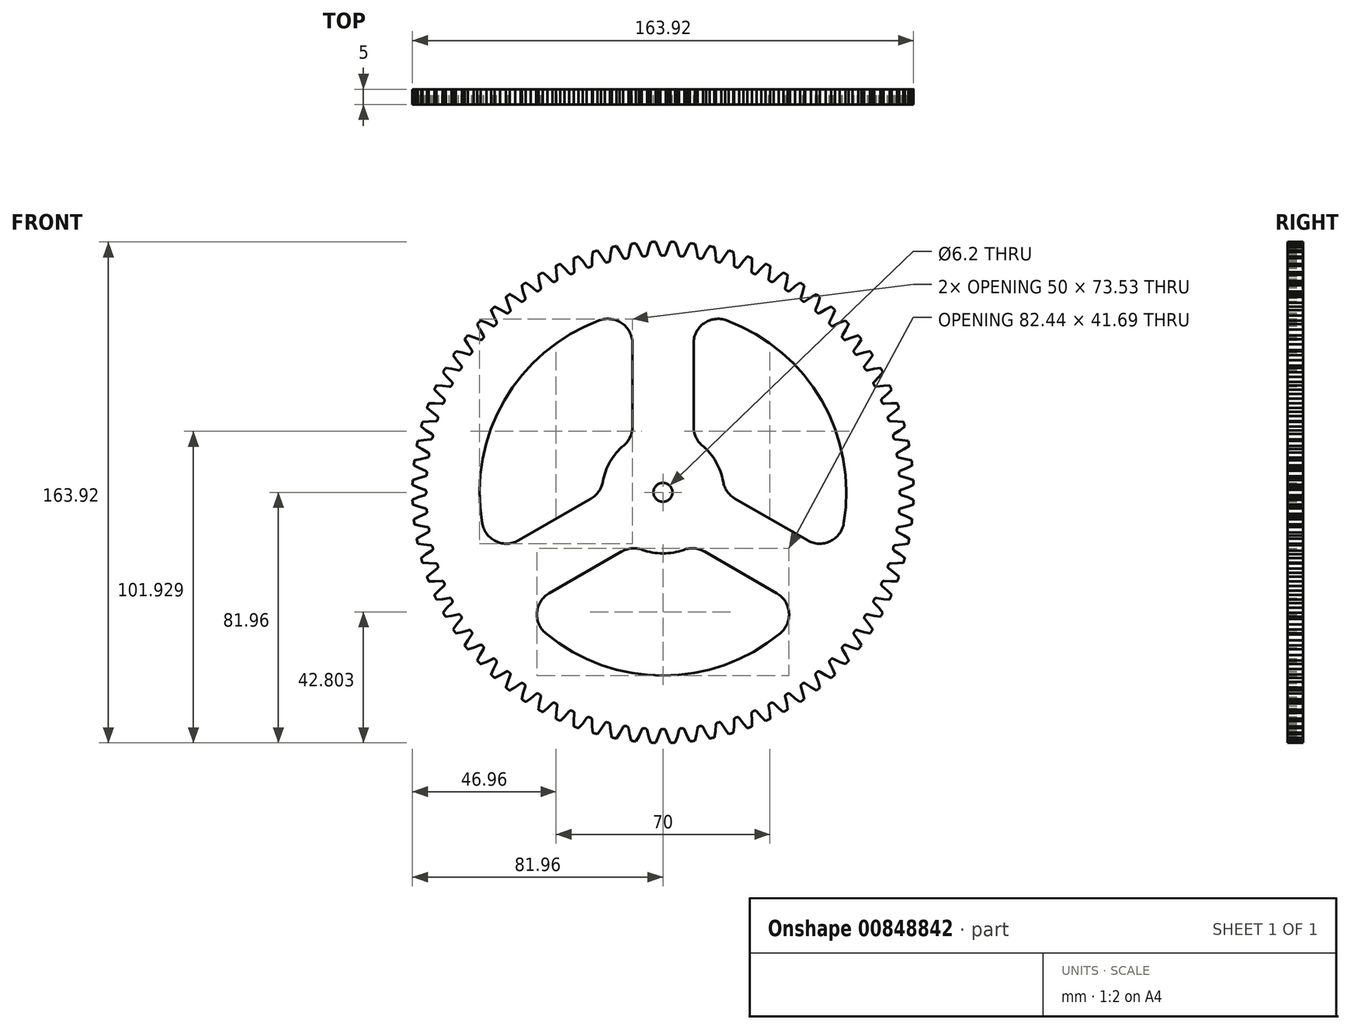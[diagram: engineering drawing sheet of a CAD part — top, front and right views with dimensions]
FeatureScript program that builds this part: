
annotation { "Feature Type Name" : "Feature", "Feature Type Description" : "" }
export const myFeature = defineFeature(function(context is Context, id is Id, definition is map)
    precondition{}
    {
        {
            var Q0;
            Q0=qCreatedBy(makeId("Front.planeOp"),FACE);
            var sketch = newSketch(context, id + "F0", { "sketchPlane" : qUnion([Q0])});
            skArc(sketch, "E0", {"start": v(-10, 21.45) * mm, "mid": v(-10.75, 18.07) * mm, "end": v(-12.86, 15.32) * mm});
            skLineSegment(sketch, "E1", {"start": v(-10, 48.79) * mm, "end": v(-10, 21.45) * mm});
            skArc(sketch, "E2", {"start": v(-20.77, 56.3) * mm, "mid": v(-13.43, 55.35) * mm, "end": v(-10, 48.79) * mm});
            skArc(sketch, "E3", {"start": v(-59.13, -10.16) * mm, "mid": v(-51.96, 30) * mm, "end": v(-20.77, 56.3) * mm});
            skArc(sketch, "E4", {"start": v(-47.25, -15.73) * mm, "mid": v(-54.65, -16.05) * mm, "end": v(-59.13, -10.16) * mm});
            skLineSegment(sketch, "E5", {"start": v(-47.25, -15.73) * mm, "end": v(-23.57, -2.06) * mm});
            skArc(sketch, "E6", {"start": v(-19.7, 3.47) * mm, "mid": v(-21.02, 0.28) * mm, "end": v(-23.57, -2.06) * mm});
            skArc(sketch, "E7", {"start": v(-19.7, 3.47) * mm, "mid": v(-17.32, 10) * mm, "end": v(-12.86, 15.32) * mm});
            skArc(sketch, "E8", {"start": v(-65.95, 40.7) * mm, "mid": v(-66.08, 40.5) * mm, "end": v(-66.2, 40.28) * mm});
            skArc(sketch, "E9", {"start": v(-65.95, 40.7) * mm, "mid": v(-65.85, 41.12) * mm, "end": v(-66.03, 41.5) * mm});
            skLineSegment(sketch, "E10", {"start": v(-67.47, 43.26) * mm, "end": v(-68.62, 44.9) * mm});
            skLineSegment(sketch, "E11", {"start": v(-66.03, 41.5) * mm, "end": v(-67.47, 43.26) * mm});
            skArc(sketch, "E12", {"start": v(-67.74, 46.22) * mm, "mid": v(-68.18, 45.56) * mm, "end": v(-68.62, 44.9) * mm});
            skLineSegment(sketch, "E13", {"start": v(-65.79, 45.78) * mm, "end": v(-67.74, 46.22) * mm});
            skLineSegment(sketch, "E14", {"start": v(-63.61, 45.12) * mm, "end": v(-65.79, 45.78) * mm});
            skArc(sketch, "E15", {"start": v(-63.61, 45.12) * mm, "mid": v(-63.19, 45.1) * mm, "end": v(-62.84, 45.35) * mm});
            skArc(sketch, "E16", {"start": v(-62.55, 45.75) * mm, "mid": v(-62.7, 45.55) * mm, "end": v(-62.84, 45.35) * mm});
            skArc(sketch, "E17", {"start": v(-62.55, 45.75) * mm, "mid": v(-62.42, 46.16) * mm, "end": v(-62.57, 46.56) * mm});
            skLineSegment(sketch, "E18", {"start": v(-63.87, 48.42) * mm, "end": v(-64.89, 50.14) * mm});
            skLineSegment(sketch, "E19", {"start": v(-62.57, 46.56) * mm, "end": v(-63.87, 48.42) * mm});
            skArc(sketch, "E20", {"start": v(-63.9, 51.39) * mm, "mid": v(-64.4, 50.77) * mm, "end": v(-64.89, 50.14) * mm});
            skLineSegment(sketch, "E21", {"start": v(-62, 50.8) * mm, "end": v(-63.9, 51.39) * mm});
            skLineSegment(sketch, "E22", {"start": v(-59.88, 49.97) * mm, "end": v(-62, 50.8) * mm});
            skArc(sketch, "E23", {"start": v(-59.88, 49.97) * mm, "mid": v(-59.46, 49.92) * mm, "end": v(-59.1, 50.14) * mm});
            skArc(sketch, "E24", {"start": v(-58.77, 50.52) * mm, "mid": v(-58.93, 50.33) * mm, "end": v(-59.1, 50.14) * mm});
            skArc(sketch, "E25", {"start": v(-58.77, 50.52) * mm, "mid": v(-58.61, 50.91) * mm, "end": v(-58.72, 51.32) * mm});
            skLineSegment(sketch, "E26", {"start": v(-59.88, 53.28) * mm, "end": v(-60.75, 55.08) * mm});
            skLineSegment(sketch, "E27", {"start": v(-58.72, 51.32) * mm, "end": v(-59.88, 53.28) * mm});
            skArc(sketch, "E28", {"start": v(-59.67, 56.24) * mm, "mid": v(-60.21, 55.66) * mm, "end": v(-60.75, 55.08) * mm});
            skLineSegment(sketch, "E29", {"start": v(-57.81, 55.51) * mm, "end": v(-59.67, 56.24) * mm});
            skLineSegment(sketch, "E30", {"start": v(-55.77, 54.51) * mm, "end": v(-57.81, 55.51) * mm});
            skArc(sketch, "E31", {"start": v(-55.77, 54.51) * mm, "mid": v(-55.36, 54.43) * mm, "end": v(-54.98, 54.63) * mm});
            skArc(sketch, "E32", {"start": v(-54.63, 54.98) * mm, "mid": v(-54.8, 54.8) * mm, "end": v(-54.98, 54.63) * mm});
            skArc(sketch, "E33", {"start": v(-54.63, 54.98) * mm, "mid": v(-54.43, 55.36) * mm, "end": v(-54.51, 55.77) * mm});
            skLineSegment(sketch, "E34", {"start": v(-55.51, 57.81) * mm, "end": v(-56.24, 59.67) * mm});
            skLineSegment(sketch, "E35", {"start": v(-54.51, 55.77) * mm, "end": v(-55.51, 57.81) * mm});
            skArc(sketch, "E36", {"start": v(-55.08, 60.75) * mm, "mid": v(-55.66, 60.21) * mm, "end": v(-56.24, 59.67) * mm});
            skLineSegment(sketch, "E37", {"start": v(-53.28, 59.88) * mm, "end": v(-55.08, 60.75) * mm});
            skLineSegment(sketch, "E38", {"start": v(-51.32, 58.72) * mm, "end": v(-53.28, 59.88) * mm});
            skArc(sketch, "E39", {"start": v(-51.32, 58.72) * mm, "mid": v(-50.91, 58.61) * mm, "end": v(-50.52, 58.77) * mm});
            skArc(sketch, "E40", {"start": v(-50.14, 59.1) * mm, "mid": v(-50.33, 58.93) * mm, "end": v(-50.52, 58.77) * mm});
            skArc(sketch, "E41", {"start": v(-50.14, 59.1) * mm, "mid": v(-49.92, 59.46) * mm, "end": v(-49.97, 59.88) * mm});
            skLineSegment(sketch, "E42", {"start": v(-50.8, 62) * mm, "end": v(-51.39, 63.9) * mm});
            skLineSegment(sketch, "E43", {"start": v(-49.97, 59.88) * mm, "end": v(-50.8, 62) * mm});
            skArc(sketch, "E44", {"start": v(-50.14, 64.89) * mm, "mid": v(-50.77, 64.4) * mm, "end": v(-51.39, 63.9) * mm});
            skLineSegment(sketch, "E45", {"start": v(-48.42, 63.87) * mm, "end": v(-50.14, 64.89) * mm});
            skLineSegment(sketch, "E46", {"start": v(-46.56, 62.57) * mm, "end": v(-48.42, 63.87) * mm});
            skArc(sketch, "E47", {"start": v(-46.56, 62.57) * mm, "mid": v(-46.16, 62.42) * mm, "end": v(-45.75, 62.55) * mm});
            skArc(sketch, "E48", {"start": v(-45.35, 62.84) * mm, "mid": v(-45.55, 62.7) * mm, "end": v(-45.75, 62.55) * mm});
            skArc(sketch, "E49", {"start": v(-45.35, 62.84) * mm, "mid": v(-45.1, 63.19) * mm, "end": v(-45.12, 63.61) * mm});
            skLineSegment(sketch, "E50", {"start": v(-45.78, 65.79) * mm, "end": v(-46.22, 67.74) * mm});
            skLineSegment(sketch, "E51", {"start": v(-45.12, 63.61) * mm, "end": v(-45.78, 65.79) * mm});
            skArc(sketch, "E52", {"start": v(-44.9, 68.62) * mm, "mid": v(-45.56, 68.18) * mm, "end": v(-46.22, 67.74) * mm});
            skLineSegment(sketch, "E53", {"start": v(-43.26, 67.47) * mm, "end": v(-44.9, 68.62) * mm});
            skLineSegment(sketch, "E54", {"start": v(-41.5, 66.03) * mm, "end": v(-43.26, 67.47) * mm});
            skArc(sketch, "E55", {"start": v(-41.5, 66.03) * mm, "mid": v(-41.12, 65.85) * mm, "end": v(-40.7, 65.95) * mm});
            skArc(sketch, "E56", {"start": v(-40.28, 66.2) * mm, "mid": v(-40.5, 66.08) * mm, "end": v(-40.7, 65.95) * mm});
            skArc(sketch, "E57", {"start": v(-40.28, 66.2) * mm, "mid": v(-40, 66.53) * mm, "end": v(-39.99, 66.96) * mm});
            skLineSegment(sketch, "E58", {"start": v(-40.48, 69.17) * mm, "end": v(-40.76, 71.15) * mm});
            skLineSegment(sketch, "E59", {"start": v(-39.99, 66.96) * mm, "end": v(-40.48, 69.17) * mm});
            skArc(sketch, "E60", {"start": v(-39.37, 71.93) * mm, "mid": v(-40.07, 71.54) * mm, "end": v(-40.76, 71.15) * mm});
            skLineSegment(sketch, "E61", {"start": v(-37.83, 70.66) * mm, "end": v(-39.37, 71.93) * mm});
            skLineSegment(sketch, "E62", {"start": v(-36.2, 69.08) * mm, "end": v(-37.83, 70.66) * mm});
            skArc(sketch, "E63", {"start": v(-36.2, 69.08) * mm, "mid": v(-35.82, 68.88) * mm, "end": v(-35.4, 68.94) * mm});
            skArc(sketch, "E64", {"start": v(-34.96, 69.17) * mm, "mid": v(-35.18, 69.05) * mm, "end": v(-35.4, 68.94) * mm});
            skArc(sketch, "E65", {"start": v(-34.96, 69.17) * mm, "mid": v(-34.66, 69.47) * mm, "end": v(-34.6, 69.89) * mm});
            skLineSegment(sketch, "E66", {"start": v(-34.93, 72.14) * mm, "end": v(-35.05, 74.13) * mm});
            skLineSegment(sketch, "E67", {"start": v(-34.6, 69.89) * mm, "end": v(-34.93, 72.14) * mm});
            skArc(sketch, "E68", {"start": v(-33.6, 74.8) * mm, "mid": v(-34.33, 74.47) * mm, "end": v(-35.05, 74.13) * mm});
            skLineSegment(sketch, "E69", {"start": v(-32.17, 73.4) * mm, "end": v(-33.6, 74.8) * mm});
            skLineSegment(sketch, "E70", {"start": v(-30.67, 71.7) * mm, "end": v(-32.17, 73.4) * mm});
            skArc(sketch, "E71", {"start": v(-30.67, 71.7) * mm, "mid": v(-30.31, 71.47) * mm, "end": v(-29.89, 71.5) * mm});
            skArc(sketch, "E72", {"start": v(-29.43, 71.7) * mm, "mid": v(-29.66, 71.6) * mm, "end": v(-29.89, 71.5) * mm});
            skArc(sketch, "E73", {"start": v(-29.43, 71.7) * mm, "mid": v(-29.1, 71.97) * mm, "end": v(-29.02, 72.39) * mm});
            skLineSegment(sketch, "E74", {"start": v(-29.16, 74.66) * mm, "end": v(-29.13, 76.65) * mm});
            skLineSegment(sketch, "E75", {"start": v(-29.02, 72.39) * mm, "end": v(-29.16, 74.66) * mm});
            skArc(sketch, "E76", {"start": v(-27.63, 77.2) * mm, "mid": v(-28.38, 76.93) * mm, "end": v(-29.13, 76.65) * mm});
            skLineSegment(sketch, "E77", {"start": v(-26.31, 75.7) * mm, "end": v(-27.63, 77.2) * mm});
            skLineSegment(sketch, "E78", {"start": v(-24.95, 73.9) * mm, "end": v(-26.31, 75.7) * mm});
            skArc(sketch, "E79", {"start": v(-24.95, 73.9) * mm, "mid": v(-24.6, 73.63) * mm, "end": v(-24.18, 73.63) * mm});
            skArc(sketch, "E80", {"start": v(-23.71, 73.78) * mm, "mid": v(-23.95, 73.7) * mm, "end": v(-24.18, 73.63) * mm});
            skArc(sketch, "E81", {"start": v(-23.71, 73.78) * mm, "mid": v(-23.37, 74.03) * mm, "end": v(-23.25, 74.44) * mm});
            skLineSegment(sketch, "E82", {"start": v(-23.21, 76.71) * mm, "end": v(-23.02, 78.7) * mm});
            skLineSegment(sketch, "E83", {"start": v(-23.25, 74.44) * mm, "end": v(-23.21, 76.71) * mm});
            skArc(sketch, "E84", {"start": v(-21.5, 79.13) * mm, "mid": v(-22.26, 78.92) * mm, "end": v(-23.02, 78.7) * mm});
            skLineSegment(sketch, "E85", {"start": v(-20.29, 77.54) * mm, "end": v(-21.5, 79.13) * mm});
            skLineSegment(sketch, "E86", {"start": v(-19.07, 75.62) * mm, "end": v(-20.29, 77.54) * mm});
            skArc(sketch, "E87", {"start": v(-19.07, 75.62) * mm, "mid": v(-18.76, 75.34) * mm, "end": v(-18.33, 75.3) * mm});
            skArc(sketch, "E88", {"start": v(-17.85, 75.42) * mm, "mid": v(-18.1, 75.36) * mm, "end": v(-18.33, 75.3) * mm});
            skArc(sketch, "E89", {"start": v(-17.85, 75.42) * mm, "mid": v(-17.5, 75.64) * mm, "end": v(-17.34, 76.04) * mm});
            skLineSegment(sketch, "E90", {"start": v(-17.12, 78.3) * mm, "end": v(-16.78, 80.27) * mm});
            skLineSegment(sketch, "E91", {"start": v(-17.34, 76.04) * mm, "end": v(-17.12, 78.3) * mm});
            skArc(sketch, "E92", {"start": v(-15.22, 80.58) * mm, "mid": v(-16, 80.42) * mm, "end": v(-16.78, 80.27) * mm});
            skLineSegment(sketch, "E93", {"start": v(-14.14, 78.9) * mm, "end": v(-15.22, 80.58) * mm});
            skLineSegment(sketch, "E94", {"start": v(-13.08, 76.88) * mm, "end": v(-14.14, 78.9) * mm});
            skArc(sketch, "E95", {"start": v(-13.08, 76.88) * mm, "mid": v(-12.79, 76.58) * mm, "end": v(-12.37, 76.5) * mm});
            skArc(sketch, "E96", {"start": v(-11.88, 76.58) * mm, "mid": v(-12.12, 76.55) * mm, "end": v(-12.37, 76.5) * mm});
            skArc(sketch, "E97", {"start": v(-11.88, 76.58) * mm, "mid": v(-11.5, 76.78) * mm, "end": v(-11.32, 77.16) * mm});
            skLineSegment(sketch, "E98", {"start": v(-10.93, 79.4) * mm, "end": v(-10.43, 81.33) * mm});
            skLineSegment(sketch, "E99", {"start": v(-11.32, 77.16) * mm, "end": v(-10.93, 79.4) * mm});
            skArc(sketch, "E100", {"start": v(-8.85, 81.52) * mm, "mid": v(-9.64, 81.43) * mm, "end": v(-10.43, 81.33) * mm});
            skLineSegment(sketch, "E101", {"start": v(-7.9, 79.76) * mm, "end": v(-8.85, 81.52) * mm});
            skLineSegment(sketch, "E102", {"start": v(-7, 77.67) * mm, "end": v(-7.9, 79.76) * mm});
            skArc(sketch, "E103", {"start": v(-7, 77.67) * mm, "mid": v(-6.74, 77.34) * mm, "end": v(-6.33, 77.24) * mm});
            skArc(sketch, "E104", {"start": v(-5.83, 77.28) * mm, "mid": v(-6.08, 77.26) * mm, "end": v(-6.33, 77.24) * mm});
            skArc(sketch, "E105", {"start": v(-5.83, 77.28) * mm, "mid": v(-5.44, 77.45) * mm, "end": v(-5.23, 77.81) * mm});
            skLineSegment(sketch, "E106", {"start": v(-4.66, 80.01) * mm, "end": v(-4.01, 81.9) * mm});
            skLineSegment(sketch, "E107", {"start": v(-5.23, 77.81) * mm, "end": v(-4.66, 80.01) * mm});
            skArc(sketch, "E108", {"start": v(-2.42, 81.96) * mm, "mid": v(-3.22, 81.94) * mm, "end": v(-4.01, 81.9) * mm});
            skLineSegment(sketch, "E109", {"start": v(-1.63, 80.13) * mm, "end": v(-2.42, 81.96) * mm});
            skLineSegment(sketch, "E110", {"start": v(-0.9, 77.98) * mm, "end": v(-1.63, 80.13) * mm});
            skArc(sketch, "E111", {"start": v(-0.9, 77.98) * mm, "mid": v(-0.65, 77.63) * mm, "end": v(-0.25, 77.5) * mm});
            skArc(sketch, "E112", {"start": v(0.25, 77.5) * mm, "mid": v(0, 77.5) * mm, "end": v(-0.25, 77.5) * mm});
            skArc(sketch, "E113", {"start": v(0.25, 77.5) * mm, "mid": v(0.65, 77.63) * mm, "end": v(0.9, 77.98) * mm});
            skLineSegment(sketch, "E114", {"start": v(1.63, 80.13) * mm, "end": v(2.42, 81.96) * mm});
            skLineSegment(sketch, "E115", {"start": v(0.9, 77.98) * mm, "end": v(1.63, 80.13) * mm});
            skArc(sketch, "E116", {"start": v(4.01, 81.9) * mm, "mid": v(3.22, 81.94) * mm, "end": v(2.42, 81.96) * mm});
            skLineSegment(sketch, "E117", {"start": v(4.66, 80.01) * mm, "end": v(4.01, 81.9) * mm});
            skLineSegment(sketch, "E118", {"start": v(5.23, 77.81) * mm, "end": v(4.66, 80.01) * mm});
            skArc(sketch, "E119", {"start": v(5.23, 77.81) * mm, "mid": v(5.44, 77.45) * mm, "end": v(5.83, 77.28) * mm});
            skArc(sketch, "E120", {"start": v(6.33, 77.24) * mm, "mid": v(6.08, 77.26) * mm, "end": v(5.83, 77.28) * mm});
            skArc(sketch, "E121", {"start": v(6.33, 77.24) * mm, "mid": v(6.74, 77.34) * mm, "end": v(7, 77.67) * mm});
            skLineSegment(sketch, "E122", {"start": v(7.9, 79.76) * mm, "end": v(8.85, 81.52) * mm});
            skLineSegment(sketch, "E123", {"start": v(7, 77.67) * mm, "end": v(7.9, 79.76) * mm});
            skArc(sketch, "E124", {"start": v(10.43, 81.33) * mm, "mid": v(9.64, 81.43) * mm, "end": v(8.85, 81.52) * mm});
            skLineSegment(sketch, "E125", {"start": v(10.93, 79.4) * mm, "end": v(10.43, 81.33) * mm});
            skLineSegment(sketch, "E126", {"start": v(11.32, 77.16) * mm, "end": v(10.93, 79.4) * mm});
            skArc(sketch, "E127", {"start": v(11.32, 77.16) * mm, "mid": v(11.5, 76.78) * mm, "end": v(11.88, 76.58) * mm});
            skArc(sketch, "E128", {"start": v(12.37, 76.5) * mm, "mid": v(12.12, 76.55) * mm, "end": v(11.88, 76.58) * mm});
            skArc(sketch, "E129", {"start": v(12.37, 76.5) * mm, "mid": v(12.79, 76.58) * mm, "end": v(13.08, 76.88) * mm});
            skLineSegment(sketch, "E130", {"start": v(14.14, 78.9) * mm, "end": v(15.22, 80.58) * mm});
            skLineSegment(sketch, "E131", {"start": v(13.08, 76.88) * mm, "end": v(14.14, 78.9) * mm});
            skArc(sketch, "E132", {"start": v(16.78, 80.27) * mm, "mid": v(16, 80.42) * mm, "end": v(15.22, 80.58) * mm});
            skLineSegment(sketch, "E133", {"start": v(17.12, 78.3) * mm, "end": v(16.78, 80.27) * mm});
            skLineSegment(sketch, "E134", {"start": v(17.34, 76.04) * mm, "end": v(17.12, 78.3) * mm});
            skArc(sketch, "E135", {"start": v(17.34, 76.04) * mm, "mid": v(17.5, 75.64) * mm, "end": v(17.85, 75.42) * mm});
            skArc(sketch, "E136", {"start": v(18.33, 75.3) * mm, "mid": v(18.1, 75.36) * mm, "end": v(17.85, 75.42) * mm});
            skArc(sketch, "E137", {"start": v(18.33, 75.3) * mm, "mid": v(18.76, 75.34) * mm, "end": v(19.07, 75.62) * mm});
            skLineSegment(sketch, "E138", {"start": v(20.29, 77.54) * mm, "end": v(21.5, 79.13) * mm});
            skLineSegment(sketch, "E139", {"start": v(19.07, 75.62) * mm, "end": v(20.29, 77.54) * mm});
            skArc(sketch, "E140", {"start": v(23.02, 78.7) * mm, "mid": v(22.26, 78.92) * mm, "end": v(21.5, 79.13) * mm});
            skLineSegment(sketch, "E141", {"start": v(23.21, 76.71) * mm, "end": v(23.02, 78.7) * mm});
            skLineSegment(sketch, "E142", {"start": v(23.25, 74.44) * mm, "end": v(23.21, 76.71) * mm});
            skArc(sketch, "E143", {"start": v(23.25, 74.44) * mm, "mid": v(23.37, 74.03) * mm, "end": v(23.71, 73.78) * mm});
            skArc(sketch, "E144", {"start": v(24.18, 73.63) * mm, "mid": v(23.95, 73.7) * mm, "end": v(23.71, 73.78) * mm});
            skArc(sketch, "E145", {"start": v(24.18, 73.63) * mm, "mid": v(24.6, 73.63) * mm, "end": v(24.95, 73.9) * mm});
            skLineSegment(sketch, "E146", {"start": v(26.31, 75.7) * mm, "end": v(27.63, 77.2) * mm});
            skLineSegment(sketch, "E147", {"start": v(24.95, 73.9) * mm, "end": v(26.31, 75.7) * mm});
            skArc(sketch, "E148", {"start": v(29.13, 76.65) * mm, "mid": v(28.38, 76.93) * mm, "end": v(27.63, 77.2) * mm});
            skLineSegment(sketch, "E149", {"start": v(29.16, 74.66) * mm, "end": v(29.13, 76.65) * mm});
            skLineSegment(sketch, "E150", {"start": v(29.02, 72.39) * mm, "end": v(29.16, 74.66) * mm});
            skArc(sketch, "E151", {"start": v(29.02, 72.39) * mm, "mid": v(29.1, 71.97) * mm, "end": v(29.43, 71.7) * mm});
            skArc(sketch, "E152", {"start": v(29.89, 71.5) * mm, "mid": v(29.66, 71.6) * mm, "end": v(29.43, 71.7) * mm});
            skArc(sketch, "E153", {"start": v(29.89, 71.5) * mm, "mid": v(30.31, 71.47) * mm, "end": v(30.67, 71.7) * mm});
            skLineSegment(sketch, "E154", {"start": v(32.17, 73.4) * mm, "end": v(33.6, 74.8) * mm});
            skLineSegment(sketch, "E155", {"start": v(30.67, 71.7) * mm, "end": v(32.17, 73.4) * mm});
            skArc(sketch, "E156", {"start": v(35.05, 74.13) * mm, "mid": v(34.33, 74.47) * mm, "end": v(33.6, 74.8) * mm});
            skLineSegment(sketch, "E157", {"start": v(34.93, 72.14) * mm, "end": v(35.05, 74.13) * mm});
            skLineSegment(sketch, "E158", {"start": v(34.6, 69.89) * mm, "end": v(34.93, 72.14) * mm});
            skArc(sketch, "E159", {"start": v(34.6, 69.89) * mm, "mid": v(34.66, 69.47) * mm, "end": v(34.96, 69.17) * mm});
            skArc(sketch, "E160", {"start": v(35.4, 68.94) * mm, "mid": v(35.18, 69.05) * mm, "end": v(34.96, 69.17) * mm});
            skArc(sketch, "E161", {"start": v(35.4, 68.94) * mm, "mid": v(35.82, 68.88) * mm, "end": v(36.2, 69.08) * mm});
            skLineSegment(sketch, "E162", {"start": v(37.83, 70.66) * mm, "end": v(39.37, 71.93) * mm});
            skLineSegment(sketch, "E163", {"start": v(36.2, 69.08) * mm, "end": v(37.83, 70.66) * mm});
            skArc(sketch, "E164", {"start": v(40.76, 71.15) * mm, "mid": v(40.07, 71.54) * mm, "end": v(39.37, 71.93) * mm});
            skLineSegment(sketch, "E165", {"start": v(40.48, 69.17) * mm, "end": v(40.76, 71.15) * mm});
            skLineSegment(sketch, "E166", {"start": v(39.99, 66.96) * mm, "end": v(40.48, 69.17) * mm});
            skArc(sketch, "E167", {"start": v(39.99, 66.96) * mm, "mid": v(40, 66.53) * mm, "end": v(40.28, 66.2) * mm});
            skArc(sketch, "E168", {"start": v(40.7, 65.95) * mm, "mid": v(40.5, 66.08) * mm, "end": v(40.28, 66.2) * mm});
            skArc(sketch, "E169", {"start": v(40.7, 65.95) * mm, "mid": v(41.12, 65.85) * mm, "end": v(41.5, 66.03) * mm});
            skLineSegment(sketch, "E170", {"start": v(43.26, 67.47) * mm, "end": v(44.9, 68.62) * mm});
            skLineSegment(sketch, "E171", {"start": v(41.5, 66.03) * mm, "end": v(43.26, 67.47) * mm});
            skArc(sketch, "E172", {"start": v(46.22, 67.74) * mm, "mid": v(45.56, 68.18) * mm, "end": v(44.9, 68.62) * mm});
            skLineSegment(sketch, "E173", {"start": v(45.78, 65.79) * mm, "end": v(46.22, 67.74) * mm});
            skLineSegment(sketch, "E174", {"start": v(45.12, 63.61) * mm, "end": v(45.78, 65.79) * mm});
            skArc(sketch, "E175", {"start": v(45.12, 63.61) * mm, "mid": v(45.1, 63.19) * mm, "end": v(45.35, 62.84) * mm});
            skArc(sketch, "E176", {"start": v(45.75, 62.55) * mm, "mid": v(45.55, 62.7) * mm, "end": v(45.35, 62.84) * mm});
            skArc(sketch, "E177", {"start": v(45.75, 62.55) * mm, "mid": v(46.16, 62.42) * mm, "end": v(46.56, 62.57) * mm});
            skLineSegment(sketch, "E178", {"start": v(48.42, 63.87) * mm, "end": v(50.14, 64.89) * mm});
            skLineSegment(sketch, "E179", {"start": v(46.56, 62.57) * mm, "end": v(48.42, 63.87) * mm});
            skArc(sketch, "E180", {"start": v(51.39, 63.9) * mm, "mid": v(50.77, 64.4) * mm, "end": v(50.14, 64.89) * mm});
            skLineSegment(sketch, "E181", {"start": v(50.8, 62) * mm, "end": v(51.39, 63.9) * mm});
            skLineSegment(sketch, "E182", {"start": v(49.97, 59.88) * mm, "end": v(50.8, 62) * mm});
            skArc(sketch, "E183", {"start": v(49.97, 59.88) * mm, "mid": v(49.92, 59.46) * mm, "end": v(50.14, 59.1) * mm});
            skArc(sketch, "E184", {"start": v(50.52, 58.77) * mm, "mid": v(50.33, 58.93) * mm, "end": v(50.14, 59.1) * mm});
            skArc(sketch, "E185", {"start": v(50.52, 58.77) * mm, "mid": v(50.91, 58.61) * mm, "end": v(51.32, 58.72) * mm});
            skLineSegment(sketch, "E186", {"start": v(53.28, 59.88) * mm, "end": v(55.08, 60.75) * mm});
            skLineSegment(sketch, "E187", {"start": v(51.32, 58.72) * mm, "end": v(53.28, 59.88) * mm});
            skArc(sketch, "E188", {"start": v(56.24, 59.67) * mm, "mid": v(55.66, 60.21) * mm, "end": v(55.08, 60.75) * mm});
            skLineSegment(sketch, "E189", {"start": v(55.51, 57.81) * mm, "end": v(56.24, 59.67) * mm});
            skLineSegment(sketch, "E190", {"start": v(54.51, 55.77) * mm, "end": v(55.51, 57.81) * mm});
            skArc(sketch, "E191", {"start": v(54.51, 55.77) * mm, "mid": v(54.43, 55.36) * mm, "end": v(54.63, 54.98) * mm});
            skArc(sketch, "E192", {"start": v(54.98, 54.63) * mm, "mid": v(54.8, 54.8) * mm, "end": v(54.63, 54.98) * mm});
            skArc(sketch, "E193", {"start": v(54.98, 54.63) * mm, "mid": v(55.36, 54.43) * mm, "end": v(55.77, 54.51) * mm});
            skLineSegment(sketch, "E194", {"start": v(57.81, 55.51) * mm, "end": v(59.67, 56.24) * mm});
            skLineSegment(sketch, "E195", {"start": v(55.77, 54.51) * mm, "end": v(57.81, 55.51) * mm});
            skArc(sketch, "E196", {"start": v(60.75, 55.08) * mm, "mid": v(60.21, 55.66) * mm, "end": v(59.67, 56.24) * mm});
            skLineSegment(sketch, "E197", {"start": v(59.88, 53.28) * mm, "end": v(60.75, 55.08) * mm});
            skLineSegment(sketch, "E198", {"start": v(58.72, 51.32) * mm, "end": v(59.88, 53.28) * mm});
            skArc(sketch, "E199", {"start": v(58.72, 51.32) * mm, "mid": v(58.61, 50.91) * mm, "end": v(58.77, 50.52) * mm});
            skArc(sketch, "E200", {"start": v(59.1, 50.14) * mm, "mid": v(58.93, 50.33) * mm, "end": v(58.77, 50.52) * mm});
            skArc(sketch, "E201", {"start": v(59.1, 50.14) * mm, "mid": v(59.46, 49.92) * mm, "end": v(59.88, 49.97) * mm});
            skLineSegment(sketch, "E202", {"start": v(62, 50.8) * mm, "end": v(63.9, 51.39) * mm});
            skLineSegment(sketch, "E203", {"start": v(59.88, 49.97) * mm, "end": v(62, 50.8) * mm});
            skArc(sketch, "E204", {"start": v(64.89, 50.14) * mm, "mid": v(64.4, 50.77) * mm, "end": v(63.9, 51.39) * mm});
            skLineSegment(sketch, "E205", {"start": v(63.87, 48.42) * mm, "end": v(64.89, 50.14) * mm});
            skLineSegment(sketch, "E206", {"start": v(62.57, 46.56) * mm, "end": v(63.87, 48.42) * mm});
            skArc(sketch, "E207", {"start": v(62.57, 46.56) * mm, "mid": v(62.42, 46.16) * mm, "end": v(62.55, 45.75) * mm});
            skArc(sketch, "E208", {"start": v(62.84, 45.35) * mm, "mid": v(62.7, 45.55) * mm, "end": v(62.55, 45.75) * mm});
            skArc(sketch, "E209", {"start": v(62.84, 45.35) * mm, "mid": v(63.19, 45.1) * mm, "end": v(63.61, 45.12) * mm});
            skLineSegment(sketch, "E210", {"start": v(65.79, 45.78) * mm, "end": v(67.74, 46.22) * mm});
            skLineSegment(sketch, "E211", {"start": v(63.61, 45.12) * mm, "end": v(65.79, 45.78) * mm});
            skArc(sketch, "E212", {"start": v(68.62, 44.9) * mm, "mid": v(68.18, 45.56) * mm, "end": v(67.74, 46.22) * mm});
            skLineSegment(sketch, "E213", {"start": v(67.47, 43.26) * mm, "end": v(68.62, 44.9) * mm});
            skLineSegment(sketch, "E214", {"start": v(66.03, 41.5) * mm, "end": v(67.47, 43.26) * mm});
            skArc(sketch, "E215", {"start": v(66.03, 41.5) * mm, "mid": v(65.85, 41.12) * mm, "end": v(65.95, 40.7) * mm});
            skArc(sketch, "E216", {"start": v(66.2, 40.28) * mm, "mid": v(66.08, 40.5) * mm, "end": v(65.95, 40.7) * mm});
            skArc(sketch, "E217", {"start": v(66.2, 40.28) * mm, "mid": v(66.53, 40) * mm, "end": v(66.96, 39.99) * mm});
            skLineSegment(sketch, "E218", {"start": v(69.17, 40.48) * mm, "end": v(71.15, 40.76) * mm});
            skLineSegment(sketch, "E219", {"start": v(66.96, 39.99) * mm, "end": v(69.17, 40.48) * mm});
            skArc(sketch, "E220", {"start": v(71.93, 39.37) * mm, "mid": v(71.54, 40.07) * mm, "end": v(71.15, 40.76) * mm});
            skLineSegment(sketch, "E221", {"start": v(70.66, 37.83) * mm, "end": v(71.93, 39.37) * mm});
            skLineSegment(sketch, "E222", {"start": v(69.08, 36.2) * mm, "end": v(70.66, 37.83) * mm});
            skArc(sketch, "E223", {"start": v(69.08, 36.2) * mm, "mid": v(68.88, 35.82) * mm, "end": v(68.94, 35.4) * mm});
            skArc(sketch, "E224", {"start": v(69.17, 34.96) * mm, "mid": v(69.05, 35.18) * mm, "end": v(68.94, 35.4) * mm});
            skArc(sketch, "E225", {"start": v(69.17, 34.96) * mm, "mid": v(69.47, 34.66) * mm, "end": v(69.89, 34.6) * mm});
            skLineSegment(sketch, "E226", {"start": v(72.14, 34.93) * mm, "end": v(74.13, 35.05) * mm});
            skLineSegment(sketch, "E227", {"start": v(69.89, 34.6) * mm, "end": v(72.14, 34.93) * mm});
            skArc(sketch, "E228", {"start": v(74.8, 33.6) * mm, "mid": v(74.47, 34.33) * mm, "end": v(74.13, 35.05) * mm});
            skLineSegment(sketch, "E229", {"start": v(73.4, 32.17) * mm, "end": v(74.8, 33.6) * mm});
            skLineSegment(sketch, "E230", {"start": v(71.7, 30.67) * mm, "end": v(73.4, 32.17) * mm});
            skArc(sketch, "E231", {"start": v(71.7, 30.67) * mm, "mid": v(71.47, 30.31) * mm, "end": v(71.5, 29.89) * mm});
            skArc(sketch, "E232", {"start": v(71.7, 29.43) * mm, "mid": v(71.6, 29.66) * mm, "end": v(71.5, 29.89) * mm});
            skArc(sketch, "E233", {"start": v(71.7, 29.43) * mm, "mid": v(71.97, 29.1) * mm, "end": v(72.39, 29.02) * mm});
            skLineSegment(sketch, "E234", {"start": v(74.66, 29.16) * mm, "end": v(76.65, 29.13) * mm});
            skLineSegment(sketch, "E235", {"start": v(72.39, 29.02) * mm, "end": v(74.66, 29.16) * mm});
            skArc(sketch, "E236", {"start": v(77.2, 27.63) * mm, "mid": v(76.93, 28.38) * mm, "end": v(76.65, 29.13) * mm});
            skLineSegment(sketch, "E237", {"start": v(75.7, 26.31) * mm, "end": v(77.2, 27.63) * mm});
            skLineSegment(sketch, "E238", {"start": v(73.9, 24.95) * mm, "end": v(75.7, 26.31) * mm});
            skArc(sketch, "E239", {"start": v(73.9, 24.95) * mm, "mid": v(73.63, 24.6) * mm, "end": v(73.63, 24.18) * mm});
            skArc(sketch, "E240", {"start": v(73.78, 23.71) * mm, "mid": v(73.7, 23.95) * mm, "end": v(73.63, 24.18) * mm});
            skArc(sketch, "E241", {"start": v(73.78, 23.71) * mm, "mid": v(74.03, 23.37) * mm, "end": v(74.44, 23.25) * mm});
            skLineSegment(sketch, "E242", {"start": v(76.71, 23.21) * mm, "end": v(78.7, 23.02) * mm});
            skLineSegment(sketch, "E243", {"start": v(74.44, 23.25) * mm, "end": v(76.71, 23.21) * mm});
            skArc(sketch, "E244", {"start": v(79.13, 21.5) * mm, "mid": v(78.92, 22.26) * mm, "end": v(78.7, 23.02) * mm});
            skLineSegment(sketch, "E245", {"start": v(77.54, 20.29) * mm, "end": v(79.13, 21.5) * mm});
            skLineSegment(sketch, "E246", {"start": v(75.62, 19.07) * mm, "end": v(77.54, 20.29) * mm});
            skArc(sketch, "E247", {"start": v(75.62, 19.07) * mm, "mid": v(75.34, 18.76) * mm, "end": v(75.3, 18.33) * mm});
            skArc(sketch, "E248", {"start": v(75.42, 17.85) * mm, "mid": v(75.36, 18.1) * mm, "end": v(75.3, 18.33) * mm});
            skArc(sketch, "E249", {"start": v(75.42, 17.85) * mm, "mid": v(75.64, 17.5) * mm, "end": v(76.04, 17.34) * mm});
            skLineSegment(sketch, "E250", {"start": v(78.3, 17.12) * mm, "end": v(80.27, 16.78) * mm});
            skLineSegment(sketch, "E251", {"start": v(76.04, 17.34) * mm, "end": v(78.3, 17.12) * mm});
            skArc(sketch, "E252", {"start": v(80.58, 15.22) * mm, "mid": v(80.42, 16) * mm, "end": v(80.27, 16.78) * mm});
            skLineSegment(sketch, "E253", {"start": v(78.9, 14.14) * mm, "end": v(80.58, 15.22) * mm});
            skLineSegment(sketch, "E254", {"start": v(76.88, 13.08) * mm, "end": v(78.9, 14.14) * mm});
            skArc(sketch, "E255", {"start": v(76.88, 13.08) * mm, "mid": v(76.58, 12.79) * mm, "end": v(76.5, 12.37) * mm});
            skArc(sketch, "E256", {"start": v(76.58, 11.88) * mm, "mid": v(76.55, 12.12) * mm, "end": v(76.5, 12.37) * mm});
            skArc(sketch, "E257", {"start": v(-56.24, -59.67) * mm, "mid": v(-55.66, -60.21) * mm, "end": v(-55.08, -60.75) * mm});
            skLineSegment(sketch, "E258", {"start": v(-51.32, -58.72) * mm, "end": v(-53.28, -59.88) * mm});
            skLineSegment(sketch, "E259", {"start": v(-53.28, -59.88) * mm, "end": v(-55.08, -60.75) * mm});
            skArc(sketch, "E260", {"start": v(-50.52, -58.77) * mm, "mid": v(-50.91, -58.61) * mm, "end": v(-51.32, -58.72) * mm});
            skArc(sketch, "E261", {"start": v(-50.52, -58.77) * mm, "mid": v(-50.33, -58.93) * mm, "end": v(-50.14, -59.1) * mm});
            skArc(sketch, "E262", {"start": v(-49.97, -59.88) * mm, "mid": v(-49.92, -59.46) * mm, "end": v(-50.14, -59.1) * mm});
            skLineSegment(sketch, "E263", {"start": v(-49.97, -59.88) * mm, "end": v(-50.8, -62) * mm});
            skLineSegment(sketch, "E264", {"start": v(-50.8, -62) * mm, "end": v(-51.39, -63.9) * mm});
            skArc(sketch, "E265", {"start": v(-51.39, -63.9) * mm, "mid": v(-50.77, -64.4) * mm, "end": v(-50.14, -64.89) * mm});
            skLineSegment(sketch, "E266", {"start": v(-46.56, -62.57) * mm, "end": v(-48.42, -63.87) * mm});
            skLineSegment(sketch, "E267", {"start": v(-48.42, -63.87) * mm, "end": v(-50.14, -64.89) * mm});
            skArc(sketch, "E268", {"start": v(-45.75, -62.55) * mm, "mid": v(-46.16, -62.42) * mm, "end": v(-46.56, -62.57) * mm});
            skArc(sketch, "E269", {"start": v(-45.75, -62.55) * mm, "mid": v(-45.55, -62.7) * mm, "end": v(-45.35, -62.84) * mm});
            skArc(sketch, "E270", {"start": v(-45.12, -63.61) * mm, "mid": v(-45.1, -63.19) * mm, "end": v(-45.35, -62.84) * mm});
            skLineSegment(sketch, "E271", {"start": v(-45.12, -63.61) * mm, "end": v(-45.78, -65.79) * mm});
            skLineSegment(sketch, "E272", {"start": v(-45.78, -65.79) * mm, "end": v(-46.22, -67.74) * mm});
            skArc(sketch, "E273", {"start": v(-46.22, -67.74) * mm, "mid": v(-45.56, -68.18) * mm, "end": v(-44.9, -68.62) * mm});
            skLineSegment(sketch, "E274", {"start": v(-41.5, -66.03) * mm, "end": v(-43.26, -67.47) * mm});
            skLineSegment(sketch, "E275", {"start": v(-43.26, -67.47) * mm, "end": v(-44.9, -68.62) * mm});
            skArc(sketch, "E276", {"start": v(-40.7, -65.95) * mm, "mid": v(-41.12, -65.85) * mm, "end": v(-41.5, -66.03) * mm});
            skArc(sketch, "E277", {"start": v(-40.7, -65.95) * mm, "mid": v(-40.5, -66.08) * mm, "end": v(-40.28, -66.2) * mm});
            skArc(sketch, "E278", {"start": v(-39.99, -66.96) * mm, "mid": v(-40, -66.53) * mm, "end": v(-40.28, -66.2) * mm});
            skLineSegment(sketch, "E279", {"start": v(-39.99, -66.96) * mm, "end": v(-40.48, -69.17) * mm});
            skLineSegment(sketch, "E280", {"start": v(-40.48, -69.17) * mm, "end": v(-40.76, -71.15) * mm});
            skArc(sketch, "E281", {"start": v(-40.76, -71.15) * mm, "mid": v(-40.07, -71.54) * mm, "end": v(-39.37, -71.93) * mm});
            skLineSegment(sketch, "E282", {"start": v(-36.2, -69.08) * mm, "end": v(-37.83, -70.66) * mm});
            skLineSegment(sketch, "E283", {"start": v(-37.83, -70.66) * mm, "end": v(-39.37, -71.93) * mm});
            skArc(sketch, "E284", {"start": v(-35.4, -68.94) * mm, "mid": v(-35.82, -68.88) * mm, "end": v(-36.2, -69.08) * mm});
            skArc(sketch, "E285", {"start": v(-35.4, -68.94) * mm, "mid": v(-35.18, -69.05) * mm, "end": v(-34.96, -69.17) * mm});
            skArc(sketch, "E286", {"start": v(-34.6, -69.89) * mm, "mid": v(-34.66, -69.47) * mm, "end": v(-34.96, -69.17) * mm});
            skLineSegment(sketch, "E287", {"start": v(-34.6, -69.89) * mm, "end": v(-34.93, -72.14) * mm});
            skLineSegment(sketch, "E288", {"start": v(-34.93, -72.14) * mm, "end": v(-35.05, -74.13) * mm});
            skArc(sketch, "E289", {"start": v(-35.05, -74.13) * mm, "mid": v(-34.33, -74.47) * mm, "end": v(-33.6, -74.8) * mm});
            skLineSegment(sketch, "E290", {"start": v(-30.67, -71.7) * mm, "end": v(-32.17, -73.4) * mm});
            skLineSegment(sketch, "E291", {"start": v(-32.17, -73.4) * mm, "end": v(-33.6, -74.8) * mm});
            skArc(sketch, "E292", {"start": v(-29.89, -71.5) * mm, "mid": v(-30.31, -71.47) * mm, "end": v(-30.67, -71.7) * mm});
            skArc(sketch, "E293", {"start": v(-29.89, -71.5) * mm, "mid": v(-29.66, -71.6) * mm, "end": v(-29.43, -71.7) * mm});
            skArc(sketch, "E294", {"start": v(-29.02, -72.39) * mm, "mid": v(-29.1, -71.97) * mm, "end": v(-29.43, -71.7) * mm});
            skLineSegment(sketch, "E295", {"start": v(-29.02, -72.39) * mm, "end": v(-29.16, -74.66) * mm});
            skLineSegment(sketch, "E296", {"start": v(-29.16, -74.66) * mm, "end": v(-29.13, -76.65) * mm});
            skArc(sketch, "E297", {"start": v(-29.13, -76.65) * mm, "mid": v(-28.38, -76.93) * mm, "end": v(-27.63, -77.2) * mm});
            skLineSegment(sketch, "E298", {"start": v(-24.95, -73.9) * mm, "end": v(-26.31, -75.7) * mm});
            skLineSegment(sketch, "E299", {"start": v(-26.31, -75.7) * mm, "end": v(-27.63, -77.2) * mm});
            skArc(sketch, "E300", {"start": v(-24.18, -73.63) * mm, "mid": v(-24.6, -73.63) * mm, "end": v(-24.95, -73.9) * mm});
            skArc(sketch, "E301", {"start": v(-24.18, -73.63) * mm, "mid": v(-23.95, -73.7) * mm, "end": v(-23.71, -73.78) * mm});
            skArc(sketch, "E302", {"start": v(-23.25, -74.44) * mm, "mid": v(-23.37, -74.03) * mm, "end": v(-23.71, -73.78) * mm});
            skLineSegment(sketch, "E303", {"start": v(-23.25, -74.44) * mm, "end": v(-23.21, -76.71) * mm});
            skLineSegment(sketch, "E304", {"start": v(-23.21, -76.71) * mm, "end": v(-23.02, -78.7) * mm});
            skArc(sketch, "E305", {"start": v(-23.02, -78.7) * mm, "mid": v(-22.26, -78.92) * mm, "end": v(-21.5, -79.13) * mm});
            skLineSegment(sketch, "E306", {"start": v(-19.07, -75.62) * mm, "end": v(-20.29, -77.54) * mm});
            skLineSegment(sketch, "E307", {"start": v(-20.29, -77.54) * mm, "end": v(-21.5, -79.13) * mm});
            skArc(sketch, "E308", {"start": v(-18.33, -75.3) * mm, "mid": v(-18.76, -75.34) * mm, "end": v(-19.07, -75.62) * mm});
            skArc(sketch, "E309", {"start": v(-18.33, -75.3) * mm, "mid": v(-18.1, -75.36) * mm, "end": v(-17.85, -75.42) * mm});
            skArc(sketch, "E310", {"start": v(-17.34, -76.04) * mm, "mid": v(-17.5, -75.64) * mm, "end": v(-17.85, -75.42) * mm});
            skLineSegment(sketch, "E311", {"start": v(-17.34, -76.04) * mm, "end": v(-17.12, -78.3) * mm});
            skLineSegment(sketch, "E312", {"start": v(-17.12, -78.3) * mm, "end": v(-16.78, -80.27) * mm});
            skArc(sketch, "E313", {"start": v(-16.78, -80.27) * mm, "mid": v(-16, -80.42) * mm, "end": v(-15.22, -80.58) * mm});
            skLineSegment(sketch, "E314", {"start": v(-13.08, -76.88) * mm, "end": v(-14.14, -78.9) * mm});
            skLineSegment(sketch, "E315", {"start": v(-14.14, -78.9) * mm, "end": v(-15.22, -80.58) * mm});
            skArc(sketch, "E316", {"start": v(-12.37, -76.5) * mm, "mid": v(-12.79, -76.58) * mm, "end": v(-13.08, -76.88) * mm});
            skArc(sketch, "E317", {"start": v(-12.37, -76.5) * mm, "mid": v(-12.12, -76.55) * mm, "end": v(-11.88, -76.58) * mm});
            skArc(sketch, "E318", {"start": v(-11.32, -77.16) * mm, "mid": v(-11.5, -76.78) * mm, "end": v(-11.88, -76.58) * mm});
            skLineSegment(sketch, "E319", {"start": v(-11.32, -77.16) * mm, "end": v(-10.93, -79.4) * mm});
            skLineSegment(sketch, "E320", {"start": v(-10.93, -79.4) * mm, "end": v(-10.43, -81.33) * mm});
            skArc(sketch, "E321", {"start": v(-10.43, -81.33) * mm, "mid": v(-9.64, -81.43) * mm, "end": v(-8.85, -81.52) * mm});
            skLineSegment(sketch, "E322", {"start": v(-7, -77.67) * mm, "end": v(-7.9, -79.76) * mm});
            skLineSegment(sketch, "E323", {"start": v(-7.9, -79.76) * mm, "end": v(-8.85, -81.52) * mm});
            skArc(sketch, "E324", {"start": v(-6.33, -77.24) * mm, "mid": v(-6.74, -77.34) * mm, "end": v(-7, -77.67) * mm});
            skArc(sketch, "E325", {"start": v(-6.33, -77.24) * mm, "mid": v(-6.08, -77.26) * mm, "end": v(-5.83, -77.28) * mm});
            skArc(sketch, "E326", {"start": v(-5.23, -77.81) * mm, "mid": v(-5.44, -77.45) * mm, "end": v(-5.83, -77.28) * mm});
            skLineSegment(sketch, "E327", {"start": v(-5.23, -77.81) * mm, "end": v(-4.66, -80.01) * mm});
            skLineSegment(sketch, "E328", {"start": v(-4.66, -80.01) * mm, "end": v(-4.01, -81.9) * mm});
            skArc(sketch, "E329", {"start": v(-4.01, -81.9) * mm, "mid": v(-3.22, -81.94) * mm, "end": v(-2.42, -81.96) * mm});
            skLineSegment(sketch, "E330", {"start": v(-0.9, -77.98) * mm, "end": v(-1.63, -80.13) * mm});
            skLineSegment(sketch, "E331", {"start": v(-1.63, -80.13) * mm, "end": v(-2.42, -81.96) * mm});
            skArc(sketch, "E332", {"start": v(-0.25, -77.5) * mm, "mid": v(-0.65, -77.63) * mm, "end": v(-0.9, -77.98) * mm});
            skArc(sketch, "E333", {"start": v(-0.25, -77.5) * mm, "mid": v(0, -77.5) * mm, "end": v(0.25, -77.5) * mm});
            skArc(sketch, "E334", {"start": v(0.9, -77.98) * mm, "mid": v(0.65, -77.63) * mm, "end": v(0.25, -77.5) * mm});
            skLineSegment(sketch, "E335", {"start": v(0.9, -77.98) * mm, "end": v(1.63, -80.13) * mm});
            skLineSegment(sketch, "E336", {"start": v(1.63, -80.13) * mm, "end": v(2.42, -81.96) * mm});
            skArc(sketch, "E337", {"start": v(2.42, -81.96) * mm, "mid": v(3.22, -81.94) * mm, "end": v(4.01, -81.9) * mm});
            skLineSegment(sketch, "E338", {"start": v(5.23, -77.81) * mm, "end": v(4.66, -80.01) * mm});
            skLineSegment(sketch, "E339", {"start": v(4.66, -80.01) * mm, "end": v(4.01, -81.9) * mm});
            skArc(sketch, "E340", {"start": v(5.83, -77.28) * mm, "mid": v(5.44, -77.45) * mm, "end": v(5.23, -77.81) * mm});
            skArc(sketch, "E341", {"start": v(5.83, -77.28) * mm, "mid": v(6.08, -77.26) * mm, "end": v(6.33, -77.24) * mm});
            skArc(sketch, "E342", {"start": v(7, -77.67) * mm, "mid": v(6.74, -77.34) * mm, "end": v(6.33, -77.24) * mm});
            skLineSegment(sketch, "E343", {"start": v(7, -77.67) * mm, "end": v(7.9, -79.76) * mm});
            skLineSegment(sketch, "E344", {"start": v(7.9, -79.76) * mm, "end": v(8.85, -81.52) * mm});
            skArc(sketch, "E345", {"start": v(8.85, -81.52) * mm, "mid": v(9.64, -81.43) * mm, "end": v(10.43, -81.33) * mm});
            skLineSegment(sketch, "E346", {"start": v(11.32, -77.16) * mm, "end": v(10.93, -79.4) * mm});
            skLineSegment(sketch, "E347", {"start": v(10.93, -79.4) * mm, "end": v(10.43, -81.33) * mm});
            skArc(sketch, "E348", {"start": v(11.88, -76.58) * mm, "mid": v(11.5, -76.78) * mm, "end": v(11.32, -77.16) * mm});
            skArc(sketch, "E349", {"start": v(11.88, -76.58) * mm, "mid": v(12.12, -76.55) * mm, "end": v(12.37, -76.5) * mm});
            skArc(sketch, "E350", {"start": v(13.08, -76.88) * mm, "mid": v(12.79, -76.58) * mm, "end": v(12.37, -76.5) * mm});
            skLineSegment(sketch, "E351", {"start": v(13.08, -76.88) * mm, "end": v(14.14, -78.9) * mm});
            skLineSegment(sketch, "E352", {"start": v(14.14, -78.9) * mm, "end": v(15.22, -80.58) * mm});
            skArc(sketch, "E353", {"start": v(15.22, -80.58) * mm, "mid": v(16, -80.42) * mm, "end": v(16.78, -80.27) * mm});
            skLineSegment(sketch, "E354", {"start": v(17.34, -76.04) * mm, "end": v(17.12, -78.3) * mm});
            skLineSegment(sketch, "E355", {"start": v(17.12, -78.3) * mm, "end": v(16.78, -80.27) * mm});
            skArc(sketch, "E356", {"start": v(17.85, -75.42) * mm, "mid": v(17.5, -75.64) * mm, "end": v(17.34, -76.04) * mm});
            skArc(sketch, "E357", {"start": v(17.85, -75.42) * mm, "mid": v(18.1, -75.36) * mm, "end": v(18.33, -75.3) * mm});
            skCircle(sketch, "E358", {"center": v(0, 0) * mm, "radius": 3.1 * mm});
            skArc(sketch, "E359", {"start": v(19.07, -75.62) * mm, "mid": v(18.76, -75.34) * mm, "end": v(18.33, -75.3) * mm});
            skArc(sketch, "E360", {"start": v(55.08, -60.75) * mm, "mid": v(55.66, -60.21) * mm, "end": v(56.24, -59.67) * mm});
            skLineSegment(sketch, "E361", {"start": v(54.51, -55.77) * mm, "end": v(55.51, -57.81) * mm});
            skLineSegment(sketch, "E362", {"start": v(55.51, -57.81) * mm, "end": v(56.24, -59.67) * mm});
            skArc(sketch, "E363", {"start": v(54.63, -54.98) * mm, "mid": v(54.43, -55.36) * mm, "end": v(54.51, -55.77) * mm});
            skArc(sketch, "E364", {"start": v(54.63, -54.98) * mm, "mid": v(54.8, -54.8) * mm, "end": v(54.98, -54.63) * mm});
            skArc(sketch, "E365", {"start": v(55.77, -54.51) * mm, "mid": v(55.36, -54.43) * mm, "end": v(54.98, -54.63) * mm});
            skLineSegment(sketch, "E366", {"start": v(55.77, -54.51) * mm, "end": v(57.81, -55.51) * mm});
            skLineSegment(sketch, "E367", {"start": v(57.81, -55.51) * mm, "end": v(59.67, -56.24) * mm});
            skArc(sketch, "E368", {"start": v(59.67, -56.24) * mm, "mid": v(60.21, -55.66) * mm, "end": v(60.75, -55.08) * mm});
            skLineSegment(sketch, "E369", {"start": v(58.72, -51.32) * mm, "end": v(59.88, -53.28) * mm});
            skLineSegment(sketch, "E370", {"start": v(59.88, -53.28) * mm, "end": v(60.75, -55.08) * mm});
            skArc(sketch, "E371", {"start": v(58.77, -50.52) * mm, "mid": v(58.61, -50.91) * mm, "end": v(58.72, -51.32) * mm});
            skArc(sketch, "E372", {"start": v(58.77, -50.52) * mm, "mid": v(58.93, -50.33) * mm, "end": v(59.1, -50.14) * mm});
            skArc(sketch, "E373", {"start": v(59.88, -49.97) * mm, "mid": v(59.46, -49.92) * mm, "end": v(59.1, -50.14) * mm});
            skLineSegment(sketch, "E374", {"start": v(59.88, -49.97) * mm, "end": v(62, -50.8) * mm});
            skLineSegment(sketch, "E375", {"start": v(62, -50.8) * mm, "end": v(63.9, -51.39) * mm});
            skArc(sketch, "E376", {"start": v(63.9, -51.39) * mm, "mid": v(64.4, -50.77) * mm, "end": v(64.89, -50.14) * mm});
            skLineSegment(sketch, "E377", {"start": v(62.57, -46.56) * mm, "end": v(63.87, -48.42) * mm});
            skLineSegment(sketch, "E378", {"start": v(63.87, -48.42) * mm, "end": v(64.89, -50.14) * mm});
            skArc(sketch, "E379", {"start": v(62.55, -45.75) * mm, "mid": v(62.42, -46.16) * mm, "end": v(62.57, -46.56) * mm});
            skArc(sketch, "E380", {"start": v(62.55, -45.75) * mm, "mid": v(62.7, -45.55) * mm, "end": v(62.84, -45.35) * mm});
            skArc(sketch, "E381", {"start": v(63.61, -45.12) * mm, "mid": v(63.19, -45.1) * mm, "end": v(62.84, -45.35) * mm});
            skLineSegment(sketch, "E382", {"start": v(63.61, -45.12) * mm, "end": v(65.79, -45.78) * mm});
            skLineSegment(sketch, "E383", {"start": v(65.79, -45.78) * mm, "end": v(67.74, -46.22) * mm});
            skArc(sketch, "E384", {"start": v(68.94, -35.4) * mm, "mid": v(69.05, -35.18) * mm, "end": v(69.17, -34.96) * mm});
            skArc(sketch, "E385", {"start": v(69.89, -34.6) * mm, "mid": v(69.47, -34.66) * mm, "end": v(69.17, -34.96) * mm});
            skLineSegment(sketch, "E386", {"start": v(69.89, -34.6) * mm, "end": v(72.14, -34.93) * mm});
            skLineSegment(sketch, "E387", {"start": v(72.14, -34.93) * mm, "end": v(74.13, -35.05) * mm});
            skArc(sketch, "E388", {"start": v(74.13, -35.05) * mm, "mid": v(74.47, -34.33) * mm, "end": v(74.8, -33.6) * mm});
            skLineSegment(sketch, "E389", {"start": v(71.7, -30.67) * mm, "end": v(73.4, -32.17) * mm});
            skArc(sketch, "E390", {"start": v(72.39, -29.02) * mm, "mid": v(71.97, -29.1) * mm, "end": v(71.7, -29.43) * mm});
            skArc(sketch, "E391", {"start": v(71.5, -29.89) * mm, "mid": v(71.6, -29.66) * mm, "end": v(71.7, -29.43) * mm});
            skArc(sketch, "E392", {"start": v(71.5, -29.89) * mm, "mid": v(71.47, -30.31) * mm, "end": v(71.7, -30.67) * mm});
            skLineSegment(sketch, "E393", {"start": v(73.4, -32.17) * mm, "end": v(74.8, -33.6) * mm});
            skArc(sketch, "E394", {"start": v(68.94, -35.4) * mm, "mid": v(68.88, -35.82) * mm, "end": v(69.08, -36.2) * mm});
            skLineSegment(sketch, "E395", {"start": v(70.66, -37.83) * mm, "end": v(71.93, -39.37) * mm});
            skLineSegment(sketch, "E396", {"start": v(69.08, -36.2) * mm, "end": v(70.66, -37.83) * mm});
            skArc(sketch, "E397", {"start": v(71.15, -40.76) * mm, "mid": v(71.54, -40.07) * mm, "end": v(71.93, -39.37) * mm});
            skLineSegment(sketch, "E398", {"start": v(69.17, -40.48) * mm, "end": v(71.15, -40.76) * mm});
            skLineSegment(sketch, "E399", {"start": v(66.96, -39.99) * mm, "end": v(69.17, -40.48) * mm});
            skArc(sketch, "E400", {"start": v(66.96, -39.99) * mm, "mid": v(66.53, -40) * mm, "end": v(66.2, -40.28) * mm});
            skArc(sketch, "E401", {"start": v(65.95, -40.7) * mm, "mid": v(66.08, -40.5) * mm, "end": v(66.2, -40.28) * mm});
            skArc(sketch, "E402", {"start": v(65.95, -40.7) * mm, "mid": v(65.85, -41.12) * mm, "end": v(66.03, -41.5) * mm});
            skLineSegment(sketch, "E403", {"start": v(67.47, -43.26) * mm, "end": v(68.62, -44.9) * mm});
            skLineSegment(sketch, "E404", {"start": v(66.03, -41.5) * mm, "end": v(67.47, -43.26) * mm});
            skArc(sketch, "E405", {"start": v(67.74, -46.22) * mm, "mid": v(68.18, -45.56) * mm, "end": v(68.62, -44.9) * mm});
            skLineSegment(sketch, "E406", {"start": v(53.28, -59.88) * mm, "end": v(55.08, -60.75) * mm});
            skLineSegment(sketch, "E407", {"start": v(51.32, -58.72) * mm, "end": v(53.28, -59.88) * mm});
            skArc(sketch, "E408", {"start": v(51.32, -58.72) * mm, "mid": v(50.91, -58.61) * mm, "end": v(50.52, -58.77) * mm});
            skArc(sketch, "E409", {"start": v(50.14, -59.1) * mm, "mid": v(50.33, -58.93) * mm, "end": v(50.52, -58.77) * mm});
            skArc(sketch, "E410", {"start": v(50.14, -59.1) * mm, "mid": v(49.92, -59.46) * mm, "end": v(49.97, -59.88) * mm});
            skLineSegment(sketch, "E411", {"start": v(50.8, -62) * mm, "end": v(51.39, -63.9) * mm});
            skLineSegment(sketch, "E412", {"start": v(49.97, -59.88) * mm, "end": v(50.8, -62) * mm});
            skArc(sketch, "E413", {"start": v(50.14, -64.89) * mm, "mid": v(50.77, -64.4) * mm, "end": v(51.39, -63.9) * mm});
            skLineSegment(sketch, "E414", {"start": v(48.42, -63.87) * mm, "end": v(50.14, -64.89) * mm});
            skLineSegment(sketch, "E415", {"start": v(46.56, -62.57) * mm, "end": v(48.42, -63.87) * mm});
            skArc(sketch, "E416", {"start": v(46.56, -62.57) * mm, "mid": v(46.16, -62.42) * mm, "end": v(45.75, -62.55) * mm});
            skArc(sketch, "E417", {"start": v(45.35, -62.84) * mm, "mid": v(45.55, -62.7) * mm, "end": v(45.75, -62.55) * mm});
            skArc(sketch, "E418", {"start": v(45.35, -62.84) * mm, "mid": v(45.1, -63.19) * mm, "end": v(45.12, -63.61) * mm});
            skLineSegment(sketch, "E419", {"start": v(45.78, -65.79) * mm, "end": v(46.22, -67.74) * mm});
            skLineSegment(sketch, "E420", {"start": v(45.12, -63.61) * mm, "end": v(45.78, -65.79) * mm});
            skArc(sketch, "E421", {"start": v(44.9, -68.62) * mm, "mid": v(45.56, -68.18) * mm, "end": v(46.22, -67.74) * mm});
            skLineSegment(sketch, "E422", {"start": v(43.26, -67.47) * mm, "end": v(44.9, -68.62) * mm});
            skLineSegment(sketch, "E423", {"start": v(41.5, -66.03) * mm, "end": v(43.26, -67.47) * mm});
            skArc(sketch, "E424", {"start": v(41.5, -66.03) * mm, "mid": v(41.12, -65.85) * mm, "end": v(40.7, -65.95) * mm});
            skArc(sketch, "E425", {"start": v(40.28, -66.2) * mm, "mid": v(40.5, -66.08) * mm, "end": v(40.7, -65.95) * mm});
            skArc(sketch, "E426", {"start": v(40.28, -66.2) * mm, "mid": v(40, -66.53) * mm, "end": v(39.99, -66.96) * mm});
            skLineSegment(sketch, "E427", {"start": v(40.48, -69.17) * mm, "end": v(40.76, -71.15) * mm});
            skLineSegment(sketch, "E428", {"start": v(39.99, -66.96) * mm, "end": v(40.48, -69.17) * mm});
            skArc(sketch, "E429", {"start": v(39.37, -71.93) * mm, "mid": v(40.07, -71.54) * mm, "end": v(40.76, -71.15) * mm});
            skLineSegment(sketch, "E430", {"start": v(37.83, -70.66) * mm, "end": v(39.37, -71.93) * mm});
            skLineSegment(sketch, "E431", {"start": v(36.2, -69.08) * mm, "end": v(37.83, -70.66) * mm});
            skArc(sketch, "E432", {"start": v(36.2, -69.08) * mm, "mid": v(35.82, -68.88) * mm, "end": v(35.4, -68.94) * mm});
            skArc(sketch, "E433", {"start": v(34.96, -69.17) * mm, "mid": v(35.18, -69.05) * mm, "end": v(35.4, -68.94) * mm});
            skArc(sketch, "E434", {"start": v(34.96, -69.17) * mm, "mid": v(34.66, -69.47) * mm, "end": v(34.6, -69.89) * mm});
            skLineSegment(sketch, "E435", {"start": v(34.93, -72.14) * mm, "end": v(35.05, -74.13) * mm});
            skLineSegment(sketch, "E436", {"start": v(34.6, -69.89) * mm, "end": v(34.93, -72.14) * mm});
            skArc(sketch, "E437", {"start": v(33.6, -74.8) * mm, "mid": v(34.33, -74.47) * mm, "end": v(35.05, -74.13) * mm});
            skLineSegment(sketch, "E438", {"start": v(32.17, -73.4) * mm, "end": v(33.6, -74.8) * mm});
            skLineSegment(sketch, "E439", {"start": v(30.67, -71.7) * mm, "end": v(32.17, -73.4) * mm});
            skArc(sketch, "E440", {"start": v(30.67, -71.7) * mm, "mid": v(30.31, -71.47) * mm, "end": v(29.89, -71.5) * mm});
            skArc(sketch, "E441", {"start": v(29.43, -71.7) * mm, "mid": v(29.66, -71.6) * mm, "end": v(29.89, -71.5) * mm});
            skArc(sketch, "E442", {"start": v(29.43, -71.7) * mm, "mid": v(29.1, -71.97) * mm, "end": v(29.02, -72.39) * mm});
            skLineSegment(sketch, "E443", {"start": v(29.16, -74.66) * mm, "end": v(29.13, -76.65) * mm});
            skLineSegment(sketch, "E444", {"start": v(29.02, -72.39) * mm, "end": v(29.16, -74.66) * mm});
            skArc(sketch, "E445", {"start": v(27.63, -77.2) * mm, "mid": v(28.38, -76.93) * mm, "end": v(29.13, -76.65) * mm});
            skLineSegment(sketch, "E446", {"start": v(26.31, -75.7) * mm, "end": v(27.63, -77.2) * mm});
            skLineSegment(sketch, "E447", {"start": v(24.95, -73.9) * mm, "end": v(26.31, -75.7) * mm});
            skArc(sketch, "E448", {"start": v(24.95, -73.9) * mm, "mid": v(24.6, -73.63) * mm, "end": v(24.18, -73.63) * mm});
            skArc(sketch, "E449", {"start": v(23.71, -73.78) * mm, "mid": v(23.95, -73.7) * mm, "end": v(24.18, -73.63) * mm});
            skArc(sketch, "E450", {"start": v(23.71, -73.78) * mm, "mid": v(23.37, -74.03) * mm, "end": v(23.25, -74.44) * mm});
            skLineSegment(sketch, "E451", {"start": v(23.21, -76.71) * mm, "end": v(23.02, -78.7) * mm});
            skLineSegment(sketch, "E452", {"start": v(23.25, -74.44) * mm, "end": v(23.21, -76.71) * mm});
            skArc(sketch, "E453", {"start": v(21.5, -79.13) * mm, "mid": v(22.26, -78.92) * mm, "end": v(23.02, -78.7) * mm});
            skLineSegment(sketch, "E454", {"start": v(20.29, -77.54) * mm, "end": v(21.5, -79.13) * mm});
            skLineSegment(sketch, "E455", {"start": v(19.07, -75.62) * mm, "end": v(20.29, -77.54) * mm});
            skLineSegment(sketch, "E456", {"start": v(-55.51, -57.81) * mm, "end": v(-56.24, -59.67) * mm});
            skLineSegment(sketch, "E457", {"start": v(-54.51, -55.77) * mm, "end": v(-55.51, -57.81) * mm});
            skArc(sketch, "E458", {"start": v(-54.51, -55.77) * mm, "mid": v(-54.43, -55.36) * mm, "end": v(-54.63, -54.98) * mm});
            skArc(sketch, "E459", {"start": v(-54.98, -54.63) * mm, "mid": v(-54.8, -54.8) * mm, "end": v(-54.63, -54.98) * mm});
            skArc(sketch, "E460", {"start": v(-54.98, -54.63) * mm, "mid": v(-55.36, -54.43) * mm, "end": v(-55.77, -54.51) * mm});
            skLineSegment(sketch, "E461", {"start": v(-57.81, -55.51) * mm, "end": v(-59.67, -56.24) * mm});
            skLineSegment(sketch, "E462", {"start": v(-55.77, -54.51) * mm, "end": v(-57.81, -55.51) * mm});
            skArc(sketch, "E463", {"start": v(-60.75, -55.08) * mm, "mid": v(-60.21, -55.66) * mm, "end": v(-59.67, -56.24) * mm});
            skLineSegment(sketch, "E464", {"start": v(-59.88, -53.28) * mm, "end": v(-60.75, -55.08) * mm});
            skLineSegment(sketch, "E465", {"start": v(-58.72, -51.32) * mm, "end": v(-59.88, -53.28) * mm});
            skArc(sketch, "E466", {"start": v(-58.72, -51.32) * mm, "mid": v(-58.61, -50.91) * mm, "end": v(-58.77, -50.52) * mm});
            skArc(sketch, "E467", {"start": v(-59.1, -50.14) * mm, "mid": v(-58.93, -50.33) * mm, "end": v(-58.77, -50.52) * mm});
            skArc(sketch, "E468", {"start": v(-59.1, -50.14) * mm, "mid": v(-59.46, -49.92) * mm, "end": v(-59.88, -49.97) * mm});
            skLineSegment(sketch, "E469", {"start": v(-62, -50.8) * mm, "end": v(-63.9, -51.39) * mm});
            skLineSegment(sketch, "E470", {"start": v(-59.88, -49.97) * mm, "end": v(-62, -50.8) * mm});
            skArc(sketch, "E471", {"start": v(-64.89, -50.14) * mm, "mid": v(-64.4, -50.77) * mm, "end": v(-63.9, -51.39) * mm});
            skLineSegment(sketch, "E472", {"start": v(-63.87, -48.42) * mm, "end": v(-64.89, -50.14) * mm});
            skLineSegment(sketch, "E473", {"start": v(-62.57, -46.56) * mm, "end": v(-63.87, -48.42) * mm});
            skArc(sketch, "E474", {"start": v(-62.57, -46.56) * mm, "mid": v(-62.42, -46.16) * mm, "end": v(-62.55, -45.75) * mm});
            skArc(sketch, "E475", {"start": v(-62.84, -45.35) * mm, "mid": v(-62.7, -45.55) * mm, "end": v(-62.55, -45.75) * mm});
            skArc(sketch, "E476", {"start": v(-62.84, -45.35) * mm, "mid": v(-63.19, -45.1) * mm, "end": v(-63.61, -45.12) * mm});
            skLineSegment(sketch, "E477", {"start": v(-65.79, -45.78) * mm, "end": v(-67.74, -46.22) * mm});
            skLineSegment(sketch, "E478", {"start": v(-63.61, -45.12) * mm, "end": v(-65.79, -45.78) * mm});
            skArc(sketch, "E479", {"start": v(-68.62, -44.9) * mm, "mid": v(-68.18, -45.56) * mm, "end": v(-67.74, -46.22) * mm});
            skLineSegment(sketch, "E480", {"start": v(-67.47, -43.26) * mm, "end": v(-68.62, -44.9) * mm});
            skLineSegment(sketch, "E481", {"start": v(-66.03, -41.5) * mm, "end": v(-67.47, -43.26) * mm});
            skArc(sketch, "E482", {"start": v(-66.03, -41.5) * mm, "mid": v(-65.85, -41.12) * mm, "end": v(-65.95, -40.7) * mm});
            skArc(sketch, "E483", {"start": v(-66.2, -40.28) * mm, "mid": v(-66.08, -40.5) * mm, "end": v(-65.95, -40.7) * mm});
            skArc(sketch, "E484", {"start": v(-66.2, -40.28) * mm, "mid": v(-66.53, -40) * mm, "end": v(-66.96, -39.99) * mm});
            skLineSegment(sketch, "E485", {"start": v(-69.17, -40.48) * mm, "end": v(-71.15, -40.76) * mm});
            skLineSegment(sketch, "E486", {"start": v(-66.96, -39.99) * mm, "end": v(-69.17, -40.48) * mm});
            skArc(sketch, "E487", {"start": v(-71.93, -39.37) * mm, "mid": v(-71.54, -40.07) * mm, "end": v(-71.15, -40.76) * mm});
            skLineSegment(sketch, "E488", {"start": v(-70.66, -37.83) * mm, "end": v(-71.93, -39.37) * mm});
            skLineSegment(sketch, "E489", {"start": v(-69.08, -36.2) * mm, "end": v(-70.66, -37.83) * mm});
            skArc(sketch, "E490", {"start": v(-69.08, -36.2) * mm, "mid": v(-68.88, -35.82) * mm, "end": v(-68.94, -35.4) * mm});
            skArc(sketch, "E491", {"start": v(-69.17, -34.96) * mm, "mid": v(-69.05, -35.18) * mm, "end": v(-68.94, -35.4) * mm});
            skArc(sketch, "E492", {"start": v(-69.17, -34.96) * mm, "mid": v(-69.47, -34.66) * mm, "end": v(-69.89, -34.6) * mm});
            skLineSegment(sketch, "E493", {"start": v(-72.14, -34.93) * mm, "end": v(-74.13, -35.05) * mm});
            skLineSegment(sketch, "E494", {"start": v(-69.89, -34.6) * mm, "end": v(-72.14, -34.93) * mm});
            skArc(sketch, "E495", {"start": v(-74.8, -33.6) * mm, "mid": v(-74.47, -34.33) * mm, "end": v(-74.13, -35.05) * mm});
            skLineSegment(sketch, "E496", {"start": v(-73.4, -32.17) * mm, "end": v(-74.8, -33.6) * mm});
            skLineSegment(sketch, "E497", {"start": v(-71.7, -30.67) * mm, "end": v(-73.4, -32.17) * mm});
            skArc(sketch, "E498", {"start": v(-71.7, -30.67) * mm, "mid": v(-71.47, -30.31) * mm, "end": v(-71.5, -29.89) * mm});
            skArc(sketch, "E499", {"start": v(-71.7, -29.43) * mm, "mid": v(-71.6, -29.66) * mm, "end": v(-71.5, -29.89) * mm});
            skArc(sketch, "E500", {"start": v(-71.7, -29.43) * mm, "mid": v(-71.97, -29.1) * mm, "end": v(-72.39, -29.02) * mm});
            skLineSegment(sketch, "E501", {"start": v(-74.66, -29.16) * mm, "end": v(-76.65, -29.13) * mm});
            skLineSegment(sketch, "E502", {"start": v(-72.39, -29.02) * mm, "end": v(-74.66, -29.16) * mm});
            skArc(sketch, "E503", {"start": v(-77.2, -27.63) * mm, "mid": v(-76.93, -28.38) * mm, "end": v(-76.65, -29.13) * mm});
            skLineSegment(sketch, "E504", {"start": v(-75.7, -26.31) * mm, "end": v(-77.2, -27.63) * mm});
            skLineSegment(sketch, "E505", {"start": v(-73.9, -24.95) * mm, "end": v(-75.7, -26.31) * mm});
            skArc(sketch, "E506", {"start": v(-73.9, -24.95) * mm, "mid": v(-73.63, -24.6) * mm, "end": v(-73.63, -24.18) * mm});
            skArc(sketch, "E507", {"start": v(-73.78, -23.71) * mm, "mid": v(-73.7, -23.95) * mm, "end": v(-73.63, -24.18) * mm});
            skArc(sketch, "E508", {"start": v(-73.78, -23.71) * mm, "mid": v(-74.03, -23.37) * mm, "end": v(-74.44, -23.25) * mm});
            skLineSegment(sketch, "E509", {"start": v(-76.71, -23.21) * mm, "end": v(-78.7, -23.02) * mm});
            skLineSegment(sketch, "E510", {"start": v(-74.44, -23.25) * mm, "end": v(-76.71, -23.21) * mm});
            skArc(sketch, "E511", {"start": v(-79.13, -21.5) * mm, "mid": v(-78.92, -22.26) * mm, "end": v(-78.7, -23.02) * mm});
            skLineSegment(sketch, "E512", {"start": v(-77.54, -20.29) * mm, "end": v(-79.13, -21.5) * mm});
            skLineSegment(sketch, "E513", {"start": v(-75.62, -19.07) * mm, "end": v(-77.54, -20.29) * mm});
            skArc(sketch, "E514", {"start": v(-75.62, -19.07) * mm, "mid": v(-75.34, -18.76) * mm, "end": v(-75.3, -18.33) * mm});
            skArc(sketch, "E515", {"start": v(-75.42, -17.85) * mm, "mid": v(-75.36, -18.1) * mm, "end": v(-75.3, -18.33) * mm});
            skArc(sketch, "E516", {"start": v(-75.42, -17.85) * mm, "mid": v(-75.64, -17.5) * mm, "end": v(-76.04, -17.34) * mm});
            skLineSegment(sketch, "E517", {"start": v(-78.3, -17.12) * mm, "end": v(-80.27, -16.78) * mm});
            skLineSegment(sketch, "E518", {"start": v(-76.04, -17.34) * mm, "end": v(-78.3, -17.12) * mm});
            skArc(sketch, "E519", {"start": v(-80.58, -15.22) * mm, "mid": v(-80.42, -16) * mm, "end": v(-80.27, -16.78) * mm});
            skLineSegment(sketch, "E520", {"start": v(-78.9, -14.14) * mm, "end": v(-80.58, -15.22) * mm});
            skLineSegment(sketch, "E521", {"start": v(-76.88, -13.08) * mm, "end": v(-78.9, -14.14) * mm});
            skArc(sketch, "E522", {"start": v(-76.88, -13.08) * mm, "mid": v(-76.58, -12.79) * mm, "end": v(-76.5, -12.37) * mm});
            skArc(sketch, "E523", {"start": v(-76.58, -11.88) * mm, "mid": v(-76.55, -12.12) * mm, "end": v(-76.5, -12.37) * mm});
            skArc(sketch, "E524", {"start": v(-76.58, -11.88) * mm, "mid": v(-76.78, -11.5) * mm, "end": v(-77.16, -11.32) * mm});
            skLineSegment(sketch, "E525", {"start": v(-79.4, -10.93) * mm, "end": v(-81.33, -10.43) * mm});
            skLineSegment(sketch, "E526", {"start": v(-77.16, -11.32) * mm, "end": v(-79.4, -10.93) * mm});
            skArc(sketch, "E527", {"start": v(-81.52, -8.85) * mm, "mid": v(-81.43, -9.64) * mm, "end": v(-81.33, -10.43) * mm});
            skLineSegment(sketch, "E528", {"start": v(-79.76, -7.9) * mm, "end": v(-81.52, -8.85) * mm});
            skLineSegment(sketch, "E529", {"start": v(-77.67, -7) * mm, "end": v(-79.76, -7.9) * mm});
            skArc(sketch, "E530", {"start": v(-77.67, -7) * mm, "mid": v(-77.34, -6.74) * mm, "end": v(-77.24, -6.33) * mm});
            skArc(sketch, "E531", {"start": v(-77.28, -5.83) * mm, "mid": v(-77.26, -6.08) * mm, "end": v(-77.24, -6.33) * mm});
            skArc(sketch, "E532", {"start": v(-77.28, -5.83) * mm, "mid": v(-77.45, -5.44) * mm, "end": v(-77.81, -5.23) * mm});
            skLineSegment(sketch, "E533", {"start": v(-80.01, -4.66) * mm, "end": v(-81.9, -4.01) * mm});
            skLineSegment(sketch, "E534", {"start": v(-77.81, -5.23) * mm, "end": v(-80.01, -4.66) * mm});
            skArc(sketch, "E535", {"start": v(-81.96, -2.42) * mm, "mid": v(-81.94, -3.22) * mm, "end": v(-81.9, -4.01) * mm});
            skLineSegment(sketch, "E536", {"start": v(-80.13, -1.63) * mm, "end": v(-81.96, -2.42) * mm});
            skLineSegment(sketch, "E537", {"start": v(-77.98, -0.9) * mm, "end": v(-80.13, -1.63) * mm});
            skArc(sketch, "E538", {"start": v(-77.98, -0.9) * mm, "mid": v(-77.63, -0.65) * mm, "end": v(-77.5, -0.25) * mm});
            skArc(sketch, "E539", {"start": v(-77.5, 0.25) * mm, "mid": v(-77.5, 0) * mm, "end": v(-77.5, -0.25) * mm});
            skArc(sketch, "E540", {"start": v(-77.5, 0.25) * mm, "mid": v(-77.63, 0.65) * mm, "end": v(-77.98, 0.9) * mm});
            skLineSegment(sketch, "E541", {"start": v(-80.13, 1.63) * mm, "end": v(-81.96, 2.42) * mm});
            skLineSegment(sketch, "E542", {"start": v(-77.98, 0.9) * mm, "end": v(-80.13, 1.63) * mm});
            skArc(sketch, "E543", {"start": v(-81.9, 4.01) * mm, "mid": v(-81.94, 3.22) * mm, "end": v(-81.96, 2.42) * mm});
            skLineSegment(sketch, "E544", {"start": v(-80.01, 4.66) * mm, "end": v(-81.9, 4.01) * mm});
            skLineSegment(sketch, "E545", {"start": v(-77.81, 5.23) * mm, "end": v(-80.01, 4.66) * mm});
            skArc(sketch, "E546", {"start": v(-77.81, 5.23) * mm, "mid": v(-77.45, 5.44) * mm, "end": v(-77.28, 5.83) * mm});
            skArc(sketch, "E547", {"start": v(-77.24, 6.33) * mm, "mid": v(-77.26, 6.08) * mm, "end": v(-77.28, 5.83) * mm});
            skArc(sketch, "E548", {"start": v(-77.24, 6.33) * mm, "mid": v(-77.34, 6.74) * mm, "end": v(-77.67, 7) * mm});
            skLineSegment(sketch, "E549", {"start": v(-79.76, 7.9) * mm, "end": v(-81.52, 8.85) * mm});
            skLineSegment(sketch, "E550", {"start": v(-77.67, 7) * mm, "end": v(-79.76, 7.9) * mm});
            skArc(sketch, "E551", {"start": v(-81.33, 10.43) * mm, "mid": v(-81.43, 9.64) * mm, "end": v(-81.52, 8.85) * mm});
            skLineSegment(sketch, "E552", {"start": v(-79.4, 10.93) * mm, "end": v(-81.33, 10.43) * mm});
            skLineSegment(sketch, "E553", {"start": v(-77.16, 11.32) * mm, "end": v(-79.4, 10.93) * mm});
            skArc(sketch, "E554", {"start": v(-77.16, 11.32) * mm, "mid": v(-76.78, 11.5) * mm, "end": v(-76.58, 11.88) * mm});
            skArc(sketch, "E555", {"start": v(-76.5, 12.37) * mm, "mid": v(-76.55, 12.12) * mm, "end": v(-76.58, 11.88) * mm});
            skArc(sketch, "E556", {"start": v(-76.5, 12.37) * mm, "mid": v(-76.58, 12.79) * mm, "end": v(-76.88, 13.08) * mm});
            skLineSegment(sketch, "E557", {"start": v(-78.9, 14.14) * mm, "end": v(-80.58, 15.22) * mm});
            skLineSegment(sketch, "E558", {"start": v(-76.88, 13.08) * mm, "end": v(-78.9, 14.14) * mm});
            skArc(sketch, "E559", {"start": v(-80.27, 16.78) * mm, "mid": v(-80.42, 16) * mm, "end": v(-80.58, 15.22) * mm});
            skLineSegment(sketch, "E560", {"start": v(-78.3, 17.12) * mm, "end": v(-80.27, 16.78) * mm});
            skLineSegment(sketch, "E561", {"start": v(-76.04, 17.34) * mm, "end": v(-78.3, 17.12) * mm});
            skArc(sketch, "E562", {"start": v(-76.04, 17.34) * mm, "mid": v(-75.64, 17.5) * mm, "end": v(-75.42, 17.85) * mm});
            skArc(sketch, "E563", {"start": v(-75.3, 18.33) * mm, "mid": v(-75.36, 18.1) * mm, "end": v(-75.42, 17.85) * mm});
            skArc(sketch, "E564", {"start": v(-75.3, 18.33) * mm, "mid": v(-75.34, 18.76) * mm, "end": v(-75.62, 19.07) * mm});
            skLineSegment(sketch, "E565", {"start": v(-77.54, 20.29) * mm, "end": v(-79.13, 21.5) * mm});
            skLineSegment(sketch, "E566", {"start": v(-75.62, 19.07) * mm, "end": v(-77.54, 20.29) * mm});
            skArc(sketch, "E567", {"start": v(-78.7, 23.02) * mm, "mid": v(-78.92, 22.26) * mm, "end": v(-79.13, 21.5) * mm});
            skLineSegment(sketch, "E568", {"start": v(-76.71, 23.21) * mm, "end": v(-78.7, 23.02) * mm});
            skLineSegment(sketch, "E569", {"start": v(-74.44, 23.25) * mm, "end": v(-76.71, 23.21) * mm});
            skArc(sketch, "E570", {"start": v(-74.44, 23.25) * mm, "mid": v(-74.03, 23.37) * mm, "end": v(-73.78, 23.71) * mm});
            skArc(sketch, "E571", {"start": v(-73.63, 24.18) * mm, "mid": v(-73.7, 23.95) * mm, "end": v(-73.78, 23.71) * mm});
            skArc(sketch, "E572", {"start": v(-73.63, 24.18) * mm, "mid": v(-73.63, 24.6) * mm, "end": v(-73.9, 24.95) * mm});
            skLineSegment(sketch, "E573", {"start": v(-75.7, 26.31) * mm, "end": v(-77.2, 27.63) * mm});
            skLineSegment(sketch, "E574", {"start": v(-73.9, 24.95) * mm, "end": v(-75.7, 26.31) * mm});
            skArc(sketch, "E575", {"start": v(-76.65, 29.13) * mm, "mid": v(-76.93, 28.38) * mm, "end": v(-77.2, 27.63) * mm});
            skLineSegment(sketch, "E576", {"start": v(-74.66, 29.16) * mm, "end": v(-76.65, 29.13) * mm});
            skLineSegment(sketch, "E577", {"start": v(-72.39, 29.02) * mm, "end": v(-74.66, 29.16) * mm});
            skArc(sketch, "E578", {"start": v(-72.39, 29.02) * mm, "mid": v(-71.97, 29.1) * mm, "end": v(-71.7, 29.43) * mm});
            skArc(sketch, "E579", {"start": v(-71.5, 29.89) * mm, "mid": v(-71.6, 29.66) * mm, "end": v(-71.7, 29.43) * mm});
            skArc(sketch, "E580", {"start": v(-71.5, 29.89) * mm, "mid": v(-71.47, 30.31) * mm, "end": v(-71.7, 30.67) * mm});
            skLineSegment(sketch, "E581", {"start": v(-73.4, 32.17) * mm, "end": v(-74.8, 33.6) * mm});
            skLineSegment(sketch, "E582", {"start": v(-71.7, 30.67) * mm, "end": v(-73.4, 32.17) * mm});
            skArc(sketch, "E583", {"start": v(-74.13, 35.05) * mm, "mid": v(-74.47, 34.33) * mm, "end": v(-74.8, 33.6) * mm});
            skLineSegment(sketch, "E584", {"start": v(-72.14, 34.93) * mm, "end": v(-74.13, 35.05) * mm});
            skLineSegment(sketch, "E585", {"start": v(-69.89, 34.6) * mm, "end": v(-72.14, 34.93) * mm});
            skArc(sketch, "E586", {"start": v(-69.89, 34.6) * mm, "mid": v(-69.47, 34.66) * mm, "end": v(-69.17, 34.96) * mm});
            skArc(sketch, "E587", {"start": v(-68.94, 35.4) * mm, "mid": v(-69.05, 35.18) * mm, "end": v(-69.17, 34.96) * mm});
            skArc(sketch, "E588", {"start": v(-68.94, 35.4) * mm, "mid": v(-68.88, 35.82) * mm, "end": v(-69.08, 36.2) * mm});
            skLineSegment(sketch, "E589", {"start": v(-70.66, 37.83) * mm, "end": v(-71.93, 39.37) * mm});
            skLineSegment(sketch, "E590", {"start": v(-69.08, 36.2) * mm, "end": v(-70.66, 37.83) * mm});
            skArc(sketch, "E591", {"start": v(-71.15, 40.76) * mm, "mid": v(-71.54, 40.07) * mm, "end": v(-71.93, 39.37) * mm});
            skLineSegment(sketch, "E592", {"start": v(-69.17, 40.48) * mm, "end": v(-71.15, 40.76) * mm});
            skLineSegment(sketch, "E593", {"start": v(-66.96, 39.99) * mm, "end": v(-69.17, 40.48) * mm});
            skArc(sketch, "E594", {"start": v(-66.96, 39.99) * mm, "mid": v(-66.53, 40) * mm, "end": v(-66.2, 40.28) * mm});
            skArc(sketch, "E595", {"start": v(59.13, -10.16) * mm, "mid": v(54.65, -16.05) * mm, "end": v(47.25, -15.73) * mm});
            skArc(sketch, "E596", {"start": v(20.77, 56.3) * mm, "mid": v(51.96, 30) * mm, "end": v(59.13, -10.16) * mm});
            skArc(sketch, "E597", {"start": v(10, 48.79) * mm, "mid": v(13.43, 55.35) * mm, "end": v(20.77, 56.3) * mm});
            skLineSegment(sketch, "E598", {"start": v(10, 48.79) * mm, "end": v(10, 21.45) * mm});
            skArc(sketch, "E599", {"start": v(12.86, 15.32) * mm, "mid": v(10.75, 18.07) * mm, "end": v(10, 21.45) * mm});
            skArc(sketch, "E600", {"start": v(12.86, 15.32) * mm, "mid": v(17.32, 10) * mm, "end": v(19.7, 3.47) * mm});
            skArc(sketch, "E601", {"start": v(23.57, -2.06) * mm, "mid": v(21.02, 0.28) * mm, "end": v(19.7, 3.47) * mm});
            skLineSegment(sketch, "E602", {"start": v(47.25, -15.73) * mm, "end": v(23.57, -2.06) * mm});
            skArc(sketch, "E603", {"start": v(37.25, -33.05) * mm, "mid": v(41.22, -39.3) * mm, "end": v(38.36, -46.13) * mm});
            skLineSegment(sketch, "E604", {"start": v(37.25, -33.05) * mm, "end": v(13.57, -19.38) * mm});
            skArc(sketch, "E605", {"start": v(6.84, -18.8) * mm, "mid": v(10.27, -18.34) * mm, "end": v(13.57, -19.38) * mm});
            skArc(sketch, "E606", {"start": v(6.84, -18.8) * mm, "mid": v(0, -20) * mm, "end": v(-6.84, -18.8) * mm});
            skArc(sketch, "E607", {"start": v(-13.57, -19.38) * mm, "mid": v(-10.27, -18.34) * mm, "end": v(-6.84, -18.8) * mm});
            skLineSegment(sketch, "E608", {"start": v(-37.25, -33.05) * mm, "end": v(-13.57, -19.38) * mm});
            skArc(sketch, "E609", {"start": v(-38.36, -46.13) * mm, "mid": v(-41.22, -39.3) * mm, "end": v(-37.25, -33.05) * mm});
            skArc(sketch, "E610", {"start": v(38.36, -46.13) * mm, "mid": v(0, -60) * mm, "end": v(-38.36, -46.13) * mm});
            skLineSegment(sketch, "E611", {"start": v(72.39, -29.02) * mm, "end": v(74.66, -29.16) * mm});
            skLineSegment(sketch, "E612", {"start": v(74.66, -29.16) * mm, "end": v(76.65, -29.13) * mm});
            skArc(sketch, "E613", {"start": v(76.65, -29.13) * mm, "mid": v(76.93, -28.38) * mm, "end": v(77.2, -27.63) * mm});
            skLineSegment(sketch, "E614", {"start": v(73.9, -24.95) * mm, "end": v(75.7, -26.31) * mm});
            skLineSegment(sketch, "E615", {"start": v(75.7, -26.31) * mm, "end": v(77.2, -27.63) * mm});
            skArc(sketch, "E616", {"start": v(73.63, -24.18) * mm, "mid": v(73.63, -24.6) * mm, "end": v(73.9, -24.95) * mm});
            skArc(sketch, "E617", {"start": v(73.63, -24.18) * mm, "mid": v(73.7, -23.95) * mm, "end": v(73.78, -23.71) * mm});
            skArc(sketch, "E618", {"start": v(74.44, -23.25) * mm, "mid": v(74.03, -23.37) * mm, "end": v(73.78, -23.71) * mm});
            skLineSegment(sketch, "E619", {"start": v(74.44, -23.25) * mm, "end": v(76.71, -23.21) * mm});
            skLineSegment(sketch, "E620", {"start": v(76.71, -23.21) * mm, "end": v(78.7, -23.02) * mm});
            skArc(sketch, "E621", {"start": v(78.7, -23.02) * mm, "mid": v(78.92, -22.26) * mm, "end": v(79.13, -21.5) * mm});
            skLineSegment(sketch, "E622", {"start": v(75.62, -19.07) * mm, "end": v(77.54, -20.29) * mm});
            skLineSegment(sketch, "E623", {"start": v(77.54, -20.29) * mm, "end": v(79.13, -21.5) * mm});
            skArc(sketch, "E624", {"start": v(75.3, -18.33) * mm, "mid": v(75.34, -18.76) * mm, "end": v(75.62, -19.07) * mm});
            skArc(sketch, "E625", {"start": v(75.3, -18.33) * mm, "mid": v(75.36, -18.1) * mm, "end": v(75.42, -17.85) * mm});
            skArc(sketch, "E626", {"start": v(76.04, -17.34) * mm, "mid": v(75.64, -17.5) * mm, "end": v(75.42, -17.85) * mm});
            skLineSegment(sketch, "E627", {"start": v(76.04, -17.34) * mm, "end": v(78.3, -17.12) * mm});
            skLineSegment(sketch, "E628", {"start": v(78.3, -17.12) * mm, "end": v(80.27, -16.78) * mm});
            skArc(sketch, "E629", {"start": v(80.27, -16.78) * mm, "mid": v(80.42, -16) * mm, "end": v(80.58, -15.22) * mm});
            skLineSegment(sketch, "E630", {"start": v(76.88, -13.08) * mm, "end": v(78.9, -14.14) * mm});
            skLineSegment(sketch, "E631", {"start": v(78.9, -14.14) * mm, "end": v(80.58, -15.22) * mm});
            skArc(sketch, "E632", {"start": v(76.5, -12.37) * mm, "mid": v(76.58, -12.79) * mm, "end": v(76.88, -13.08) * mm});
            skArc(sketch, "E633", {"start": v(76.5, -12.37) * mm, "mid": v(76.55, -12.12) * mm, "end": v(76.58, -11.88) * mm});
            skArc(sketch, "E634", {"start": v(77.16, -11.32) * mm, "mid": v(76.78, -11.5) * mm, "end": v(76.58, -11.88) * mm});
            skLineSegment(sketch, "E635", {"start": v(77.16, -11.32) * mm, "end": v(79.4, -10.93) * mm});
            skLineSegment(sketch, "E636", {"start": v(79.4, -10.93) * mm, "end": v(81.33, -10.43) * mm});
            skArc(sketch, "E637", {"start": v(81.33, -10.43) * mm, "mid": v(81.43, -9.64) * mm, "end": v(81.52, -8.85) * mm});
            skLineSegment(sketch, "E638", {"start": v(77.67, -7) * mm, "end": v(79.76, -7.9) * mm});
            skLineSegment(sketch, "E639", {"start": v(79.76, -7.9) * mm, "end": v(81.52, -8.85) * mm});
            skArc(sketch, "E640", {"start": v(77.24, -6.33) * mm, "mid": v(77.34, -6.74) * mm, "end": v(77.67, -7) * mm});
            skArc(sketch, "E641", {"start": v(77.24, -6.33) * mm, "mid": v(77.26, -6.08) * mm, "end": v(77.28, -5.83) * mm});
            skArc(sketch, "E642", {"start": v(77.81, -5.23) * mm, "mid": v(77.45, -5.44) * mm, "end": v(77.28, -5.83) * mm});
            skLineSegment(sketch, "E643", {"start": v(77.81, -5.23) * mm, "end": v(80.01, -4.66) * mm});
            skLineSegment(sketch, "E644", {"start": v(80.01, -4.66) * mm, "end": v(81.9, -4.01) * mm});
            skArc(sketch, "E645", {"start": v(81.9, -4.01) * mm, "mid": v(81.94, -3.22) * mm, "end": v(81.96, -2.42) * mm});
            skLineSegment(sketch, "E646", {"start": v(77.98, -0.9) * mm, "end": v(80.13, -1.63) * mm});
            skLineSegment(sketch, "E647", {"start": v(80.13, -1.63) * mm, "end": v(81.96, -2.42) * mm});
            skArc(sketch, "E648", {"start": v(77.5, -0.25) * mm, "mid": v(77.63, -0.65) * mm, "end": v(77.98, -0.9) * mm});
            skArc(sketch, "E649", {"start": v(77.5, -0.25) * mm, "mid": v(77.5, 0) * mm, "end": v(77.5, 0.25) * mm});
            skArc(sketch, "E650", {"start": v(77.98, 0.9) * mm, "mid": v(77.63, 0.65) * mm, "end": v(77.5, 0.25) * mm});
            skLineSegment(sketch, "E651", {"start": v(77.98, 0.9) * mm, "end": v(80.13, 1.63) * mm});
            skLineSegment(sketch, "E652", {"start": v(80.13, 1.63) * mm, "end": v(81.96, 2.42) * mm});
            skArc(sketch, "E653", {"start": v(81.96, 2.42) * mm, "mid": v(81.94, 3.22) * mm, "end": v(81.9, 4.01) * mm});
            skLineSegment(sketch, "E654", {"start": v(77.81, 5.23) * mm, "end": v(80.01, 4.66) * mm});
            skLineSegment(sketch, "E655", {"start": v(80.01, 4.66) * mm, "end": v(81.9, 4.01) * mm});
            skArc(sketch, "E656", {"start": v(77.28, 5.83) * mm, "mid": v(77.45, 5.44) * mm, "end": v(77.81, 5.23) * mm});
            skArc(sketch, "E657", {"start": v(77.28, 5.83) * mm, "mid": v(77.26, 6.08) * mm, "end": v(77.24, 6.33) * mm});
            skArc(sketch, "E658", {"start": v(77.67, 7) * mm, "mid": v(77.34, 6.74) * mm, "end": v(77.24, 6.33) * mm});
            skLineSegment(sketch, "E659", {"start": v(77.67, 7) * mm, "end": v(79.76, 7.9) * mm});
            skLineSegment(sketch, "E660", {"start": v(79.76, 7.9) * mm, "end": v(81.52, 8.85) * mm});
            skArc(sketch, "E661", {"start": v(81.52, 8.85) * mm, "mid": v(81.43, 9.64) * mm, "end": v(81.33, 10.43) * mm});
            skLineSegment(sketch, "E662", {"start": v(77.16, 11.32) * mm, "end": v(79.4, 10.93) * mm});
            skLineSegment(sketch, "E663", {"start": v(79.4, 10.93) * mm, "end": v(81.33, 10.43) * mm});
            skArc(sketch, "E664", {"start": v(76.58, 11.88) * mm, "mid": v(76.78, 11.5) * mm, "end": v(77.16, 11.32) * mm});
            skSolve(sketch);
        }
        {
            var Q0;
            Q0 = qSketchRegion(id + "F0", true);
            extrude(context, id + "F1", {"entities" : qUnion([Q0]), "depth" : 5 * mm, "offsetDistance" : 25 * mm});
        }
    });
